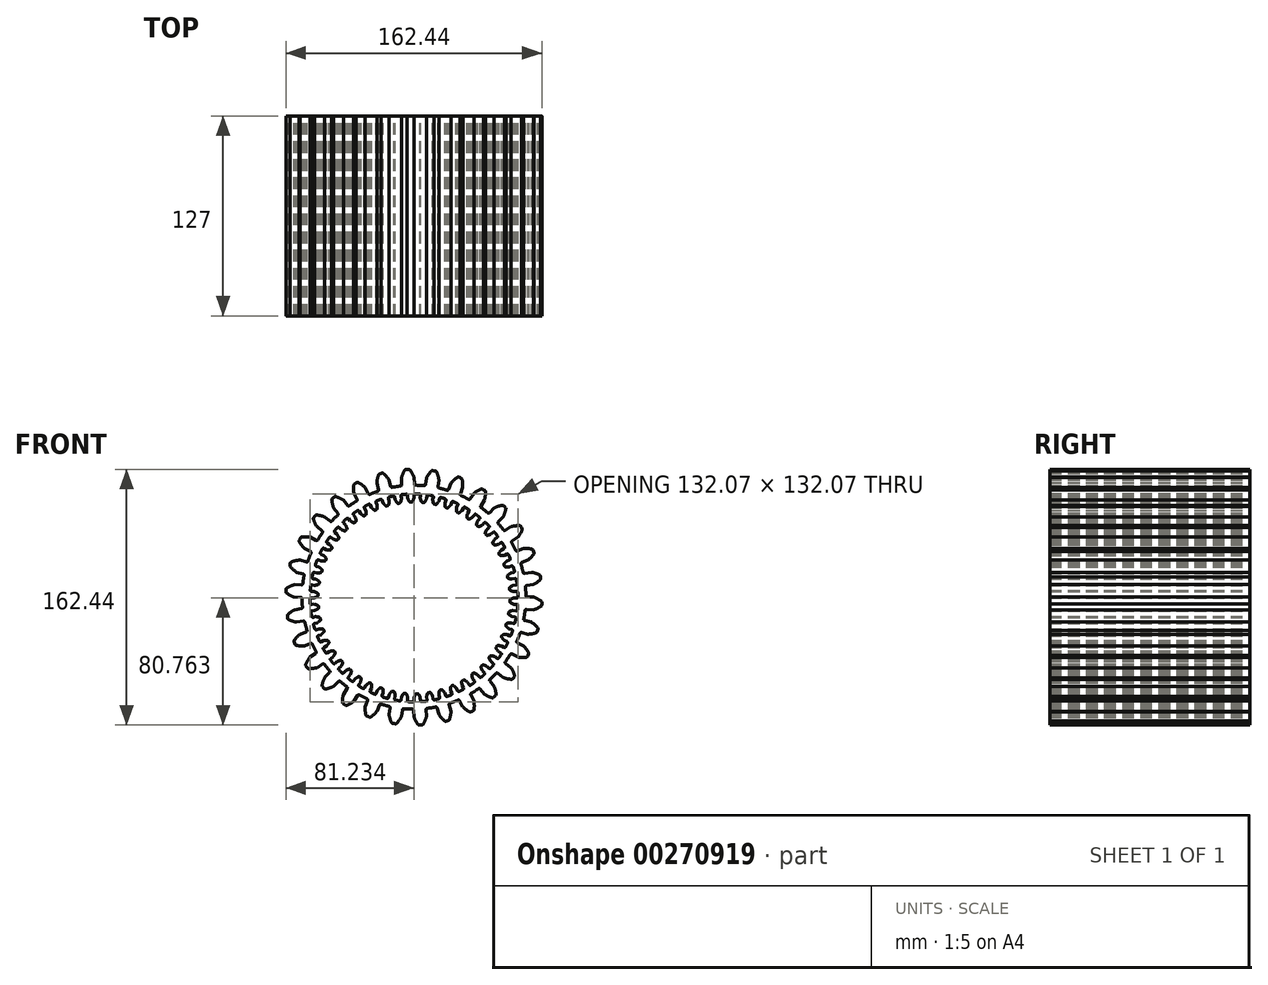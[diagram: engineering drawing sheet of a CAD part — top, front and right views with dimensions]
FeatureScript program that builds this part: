
annotation { "Feature Type Name" : "Feature", "Feature Type Description" : "" }
export const myFeature = defineFeature(function(context is Context, id is Id, definition is map)
    precondition{}
    {
        {
            var Q0;
            Q0=qCreatedBy(makeId("Front.planeOp"),FACE);
            var sketch = newSketch(context, id + "F0", { "sketchPlane" : qUnion([Q0])});
            skArc(sketch, "E0", {"start": v(-8.4, 70.62) * mm, "mid": v(-11.1, 70.25) * mm, "end": v(-13.76, 69.78) * mm});
            skArc(sketch, "E1.trimOffspring", {"start": v(0, 76.2) * mm, "mid": v(-1.15, 78.65) * mm, "end": v(-2.65, 80.92) * mm});
            skLineSegment(sketch, "E2", {"start": v(-3.28, 81.21) * mm, "end": v(-4.25, 81.18) * mm});
            skLineSegment(sketch, "E3", {"start": v(0, 76.2) * mm, "end": v(0.23, 71.9) * mm});
            skLineSegment(sketch, "E4.MirrorCS", {"start": v(-5.23, 81.11) * mm, "end": v(-4.25, 81.18) * mm});
            skArc(sketch, "E5.MirrorCS", {"start": v(-7.97, 75.78) * mm, "mid": v(-7.07, 78.34) * mm, "end": v(-5.83, 80.75) * mm});
            skLineSegment(sketch, "E6.MirrorCS", {"start": v(-7.97, 75.78) * mm, "end": v(-7.74, 71.42) * mm});
            skPoint(sketch, "E7.visualSharp", {"position": v(0.27, 71.12) * mm});
            skArc(sketch, "E7.filletArc", {"start": v(0.23, 71.9) * mm, "mid": v(0.48, 71.35) * mm, "end": v(1.05, 71.11) * mm});
            skPoint(sketch, "E8.visualSharp", {"position": v(-7.7, 70.7) * mm});
            skArc(sketch, "E8.filletArc", {"start": v(-8.4, 70.62) * mm, "mid": v(-7.91, 70.89) * mm, "end": v(-7.74, 71.42) * mm});
            skPoint(sketch, "E9.visualSharp", {"position": v(-5.62, 81.09) * mm});
            skArc(sketch, "E9.filletArc", {"start": v(-5.23, 81.11) * mm, "mid": v(-5.57, 81) * mm, "end": v(-5.83, 80.75) * mm});
            skPoint(sketch, "E10.visualSharp", {"position": v(-2.89, 81.23) * mm});
            skArc(sketch, "E10.filletArc", {"start": v(-2.65, 80.92) * mm, "mid": v(-2.93, 81.14) * mm, "end": v(-3.28, 81.21) * mm});
            skLineSegment(sketch, "E11.1.0", {"start": v(-21.98, 78.25) * mm, "end": v(-21.04, 78.52) * mm});
            skArc(sketch, "E11.1.1", {"start": v(-21.98, 78.25) * mm, "mid": v(-22.3, 78.08) * mm, "end": v(-22.49, 77.77) * mm});
            skLineSegment(sketch, "E11.1.2", {"start": v(-20.1, 78.76) * mm, "end": v(-21.04, 78.52) * mm});
            skArc(sketch, "E11.1.3", {"start": v(-19.41, 78.6) * mm, "mid": v(-19.73, 78.76) * mm, "end": v(-20.1, 78.76) * mm});
            skArc(sketch, "E11.1.4", {"start": v(-15.84, 74.53) * mm, "mid": v(-17.48, 76.7) * mm, "end": v(-19.41, 78.6) * mm});
            skLineSegment(sketch, "E11.1.5", {"start": v(-15.84, 74.53) * mm, "end": v(-14.73, 70.38) * mm});
            skLineSegment(sketch, "E11.1.6", {"start": v(-23.55, 72.47) * mm, "end": v(-22.42, 68.25) * mm});
            skArc(sketch, "E11.1.7", {"start": v(-22.9, 67.33) * mm, "mid": v(-22.48, 67.7) * mm, "end": v(-22.42, 68.25) * mm});
            skArc(sketch, "E11.1.8", {"start": v(-14.73, 70.38) * mm, "mid": v(-14.36, 69.89) * mm, "end": v(-13.76, 69.78) * mm});
            skArc(sketch, "E11.1.9", {"start": v(-23.55, 72.47) * mm, "mid": v(-23.2, 75.16) * mm, "end": v(-22.49, 77.77) * mm});
            skLineSegment(sketch, "E11.2.0", {"start": v(-37.77, 71.97) * mm, "end": v(-36.9, 72.43) * mm});
            skArc(sketch, "E11.2.1", {"start": v(-37.77, 71.97) * mm, "mid": v(-38.04, 71.73) * mm, "end": v(-38.17, 71.4) * mm});
            skLineSegment(sketch, "E11.2.2", {"start": v(-36.03, 72.86) * mm, "end": v(-36.9, 72.43) * mm});
            skArc(sketch, "E11.2.3", {"start": v(-35.33, 72.84) * mm, "mid": v(-35.68, 72.94) * mm, "end": v(-36.03, 72.86) * mm});
            skArc(sketch, "E11.2.4", {"start": v(-31, 69.61) * mm, "mid": v(-33.05, 71.38) * mm, "end": v(-35.33, 72.84) * mm});
            skLineSegment(sketch, "E11.2.5", {"start": v(-31, 69.61) * mm, "end": v(-29.04, 65.78) * mm});
            skLineSegment(sketch, "E11.2.6", {"start": v(-38.1, 66) * mm, "end": v(-36.12, 62.1) * mm});
            skArc(sketch, "E11.2.7", {"start": v(-36.4, 61.1) * mm, "mid": v(-36.06, 61.54) * mm, "end": v(-36.12, 62.1) * mm});
            skArc(sketch, "E11.2.8", {"start": v(-29.04, 65.78) * mm, "mid": v(-28.58, 65.37) * mm, "end": v(-27.97, 65.4) * mm});
            skArc(sketch, "E11.2.9", {"start": v(-38.1, 66) * mm, "mid": v(-38.33, 68.7) * mm, "end": v(-38.17, 71.4) * mm});
            skLineSegment(sketch, "E12.1.3.0", {"start": v(-51.9, 62.55) * mm, "end": v(-51.16, 63.18) * mm});
            skArc(sketch, "E12.3.3.0", {"start": v(-51.9, 62.55) * mm, "mid": v(-52.12, 62.26) * mm, "end": v(-52.18, 61.9) * mm});
            skLineSegment(sketch, "E12.7.3.0", {"start": v(-50.39, 63.78) * mm, "end": v(-51.16, 63.18) * mm});
            skArc(sketch, "E12.10.3.0", {"start": v(-49.7, 63.9) * mm, "mid": v(-50.06, 63.93) * mm, "end": v(-50.39, 63.78) * mm});
            skArc(sketch, "E12.14.3.0", {"start": v(-44.79, 61.65) * mm, "mid": v(-47.17, 62.95) * mm, "end": v(-49.7, 63.9) * mm});
            skLineSegment(sketch, "E12.18.3.0", {"start": v(-44.79, 61.65) * mm, "end": v(-42.08, 58.3) * mm});
            skLineSegment(sketch, "E12.21.3.0", {"start": v(-50.99, 56.63) * mm, "end": v(-48.24, 53.23) * mm});
            skArc(sketch, "E12.24.3.0", {"start": v(-48.31, 52.2) * mm, "mid": v(-48.07, 52.7) * mm, "end": v(-48.24, 53.23) * mm});
            skArc(sketch, "E12.28.3.0", {"start": v(-42.08, 58.3) * mm, "mid": v(-41.55, 58) * mm, "end": v(-40.95, 58.15) * mm});
            skArc(sketch, "E12.32.3.0", {"start": v(-50.99, 56.63) * mm, "mid": v(-51.77, 59.22) * mm, "end": v(-52.18, 61.9) * mm});
            skLineSegment(sketch, "E12.1.4.0", {"start": v(-63.78, 50.39) * mm, "end": v(-63.18, 51.16) * mm});
            skArc(sketch, "E12.3.4.0", {"start": v(-63.78, 50.39) * mm, "mid": v(-63.93, 50.06) * mm, "end": v(-63.9, 49.7) * mm});
            skLineSegment(sketch, "E12.7.4.0", {"start": v(-62.55, 51.9) * mm, "end": v(-63.18, 51.16) * mm});
            skArc(sketch, "E12.10.4.0", {"start": v(-61.9, 52.18) * mm, "mid": v(-62.26, 52.12) * mm, "end": v(-62.55, 51.9) * mm});
            skArc(sketch, "E12.14.4.0", {"start": v(-56.63, 50.99) * mm, "mid": v(-59.22, 51.77) * mm, "end": v(-61.9, 52.18) * mm});
            skLineSegment(sketch, "E12.18.4.0", {"start": v(-56.63, 50.99) * mm, "end": v(-53.28, 48.28) * mm});
            skLineSegment(sketch, "E12.21.4.0", {"start": v(-61.65, 44.79) * mm, "end": v(-58.25, 42.04) * mm});
            skArc(sketch, "E12.24.4.0", {"start": v(-58.1, 41) * mm, "mid": v(-57.98, 41.55) * mm, "end": v(-58.25, 42.04) * mm});
            skArc(sketch, "E12.28.4.0", {"start": v(-53.28, 48.28) * mm, "mid": v(-52.7, 48.1) * mm, "end": v(-52.15, 48.36) * mm});
            skArc(sketch, "E12.32.4.0", {"start": v(-61.65, 44.79) * mm, "mid": v(-62.95, 47.17) * mm, "end": v(-63.9, 49.7) * mm});
            skLineSegment(sketch, "E12.1.5.0", {"start": v(-72.86, 36.03) * mm, "end": v(-72.43, 36.9) * mm});
            skArc(sketch, "E12.3.5.0", {"start": v(-72.86, 36.03) * mm, "mid": v(-72.94, 35.68) * mm, "end": v(-72.84, 35.33) * mm});
            skLineSegment(sketch, "E12.7.5.0", {"start": v(-71.97, 37.77) * mm, "end": v(-72.43, 36.9) * mm});
            skArc(sketch, "E12.10.5.0", {"start": v(-71.4, 38.17) * mm, "mid": v(-71.73, 38.04) * mm, "end": v(-71.97, 37.77) * mm});
            skArc(sketch, "E12.14.5.0", {"start": v(-66, 38.1) * mm, "mid": v(-68.7, 38.33) * mm, "end": v(-71.4, 38.17) * mm});
            skLineSegment(sketch, "E12.18.5.0", {"start": v(-66, 38.1) * mm, "end": v(-62.16, 36.15) * mm});
            skLineSegment(sketch, "E12.21.5.0", {"start": v(-69.61, 31) * mm, "end": v(-65.72, 29) * mm});
            skArc(sketch, "E12.24.5.0", {"start": v(-65.36, 28.03) * mm, "mid": v(-65.35, 28.59) * mm, "end": v(-65.72, 29) * mm});
            skArc(sketch, "E12.28.5.0", {"start": v(-62.16, 36.15) * mm, "mid": v(-61.55, 36.09) * mm, "end": v(-61.06, 36.46) * mm});
            skArc(sketch, "E12.32.5.0", {"start": v(-69.61, 31) * mm, "mid": v(-71.38, 33.05) * mm, "end": v(-72.84, 35.33) * mm});
            skLineSegment(sketch, "E12.1.6.0", {"start": v(-78.76, 20.1) * mm, "end": v(-78.52, 21.04) * mm});
            skArc(sketch, "E12.3.6.0", {"start": v(-78.76, 20.1) * mm, "mid": v(-78.76, 19.73) * mm, "end": v(-78.6, 19.41) * mm});
            skLineSegment(sketch, "E12.7.6.0", {"start": v(-78.25, 21.98) * mm, "end": v(-78.52, 21.04) * mm});
            skArc(sketch, "E12.10.6.0", {"start": v(-77.77, 22.49) * mm, "mid": v(-78.08, 22.3) * mm, "end": v(-78.25, 21.98) * mm});
            skArc(sketch, "E12.14.6.0", {"start": v(-72.47, 23.55) * mm, "mid": v(-75.16, 23.2) * mm, "end": v(-77.77, 22.49) * mm});
            skLineSegment(sketch, "E12.18.6.0", {"start": v(-72.47, 23.55) * mm, "end": v(-68.32, 22.43) * mm});
            skLineSegment(sketch, "E12.21.6.0", {"start": v(-74.53, 15.84) * mm, "end": v(-70.31, 14.71) * mm});
            skArc(sketch, "E12.24.6.0", {"start": v(-69.76, 13.83) * mm, "mid": v(-69.86, 14.38) * mm, "end": v(-70.31, 14.71) * mm});
            skArc(sketch, "E12.28.6.0", {"start": v(-68.32, 22.43) * mm, "mid": v(-67.7, 22.5) * mm, "end": v(-67.3, 22.97) * mm});
            skArc(sketch, "E12.32.6.0", {"start": v(-74.53, 15.84) * mm, "mid": v(-76.7, 17.48) * mm, "end": v(-78.6, 19.41) * mm});
            skLineSegment(sketch, "E12.1.7.0", {"start": v(-81.21, 3.28) * mm, "end": v(-81.18, 4.25) * mm});
            skArc(sketch, "E12.3.7.0", {"start": v(-81.21, 3.28) * mm, "mid": v(-81.14, 2.93) * mm, "end": v(-80.92, 2.65) * mm});
            skLineSegment(sketch, "E12.7.7.0", {"start": v(-81.11, 5.23) * mm, "end": v(-81.18, 4.25) * mm});
            skArc(sketch, "E12.10.7.0", {"start": v(-80.75, 5.83) * mm, "mid": v(-81, 5.57) * mm, "end": v(-81.11, 5.23) * mm});
            skArc(sketch, "E12.14.7.0", {"start": v(-75.78, 7.97) * mm, "mid": v(-78.34, 7.07) * mm, "end": v(-80.75, 5.83) * mm});
            skLineSegment(sketch, "E12.18.7.0", {"start": v(-75.78, 7.97) * mm, "end": v(-71.49, 7.74) * mm});
            skLineSegment(sketch, "E12.21.7.0", {"start": v(-76.2, 0) * mm, "end": v(-71.84, -0.23) * mm});
            skArc(sketch, "E12.24.7.0", {"start": v(-71.11, -0.98) * mm, "mid": v(-71.33, -0.46) * mm, "end": v(-71.84, -0.23) * mm});
            skArc(sketch, "E12.28.7.0", {"start": v(-71.49, 7.74) * mm, "mid": v(-70.9, 7.94) * mm, "end": v(-70.61, 8.48) * mm});
            skArc(sketch, "E12.32.7.0", {"start": v(-76.2, 0) * mm, "mid": v(-78.65, 1.15) * mm, "end": v(-80.92, 2.65) * mm});
            skLineSegment(sketch, "E12.1.8.0", {"start": v(-80.12, -13.68) * mm, "end": v(-80.3, -12.72) * mm});
            skArc(sketch, "E12.3.8.0", {"start": v(-80.12, -13.68) * mm, "mid": v(-79.98, -14) * mm, "end": v(-79.7, -14.24) * mm});
            skLineSegment(sketch, "E12.7.8.0", {"start": v(-80.43, -11.75) * mm, "end": v(-80.3, -12.72) * mm});
            skArc(sketch, "E12.10.8.0", {"start": v(-80.2, -11.09) * mm, "mid": v(-80.4, -11.4) * mm, "end": v(-80.43, -11.75) * mm});
            skArc(sketch, "E12.14.8.0", {"start": v(-75.78, -7.97) * mm, "mid": v(-78.1, -9.37) * mm, "end": v(-80.2, -11.09) * mm});
            skLineSegment(sketch, "E12.18.8.0", {"start": v(-75.78, -7.97) * mm, "end": v(-71.53, -7.3) * mm});
            skLineSegment(sketch, "E12.21.8.0", {"start": v(-74.53, -15.84) * mm, "end": v(-70.22, -15.16) * mm});
            skArc(sketch, "E12.24.8.0", {"start": v(-69.36, -15.74) * mm, "mid": v(-69.67, -15.28) * mm, "end": v(-70.22, -15.16) * mm});
            skArc(sketch, "E12.28.8.0", {"start": v(-71.53, -7.3) * mm, "mid": v(-71, -6.98) * mm, "end": v(-70.83, -6.4) * mm});
            skArc(sketch, "E12.32.8.0", {"start": v(-74.53, -15.84) * mm, "mid": v(-77.17, -15.22) * mm, "end": v(-79.7, -14.24) * mm});
            skLineSegment(sketch, "E12.1.9.0", {"start": v(-75.53, -30.04) * mm, "end": v(-75.9, -29.13) * mm});
            skArc(sketch, "E12.3.9.0", {"start": v(-75.53, -30.04) * mm, "mid": v(-75.32, -30.33) * mm, "end": v(-75, -30.5) * mm});
            skLineSegment(sketch, "E12.7.9.0", {"start": v(-76.23, -28.21) * mm, "end": v(-75.9, -29.13) * mm});
            skArc(sketch, "E12.10.9.0", {"start": v(-76.14, -27.52) * mm, "mid": v(-76.27, -27.86) * mm, "end": v(-76.23, -28.21) * mm});
            skArc(sketch, "E12.14.9.0", {"start": v(-72.47, -23.55) * mm, "mid": v(-74.45, -25.4) * mm, "end": v(-76.14, -27.52) * mm});
            skLineSegment(sketch, "E12.18.9.0", {"start": v(-72.47, -23.55) * mm, "end": v(-68.45, -22) * mm});
            skLineSegment(sketch, "E12.21.9.0", {"start": v(-69.61, -31) * mm, "end": v(-65.53, -29.43) * mm});
            skArc(sketch, "E12.24.9.0", {"start": v(-64.57, -29.82) * mm, "mid": v(-64.97, -29.43) * mm, "end": v(-65.53, -29.43) * mm});
            skArc(sketch, "E12.28.9.0", {"start": v(-68.45, -22) * mm, "mid": v(-68, -21.6) * mm, "end": v(-67.96, -20.98) * mm});
            skArc(sketch, "E12.32.9.0", {"start": v(-69.61, -31) * mm, "mid": v(-72.32, -30.94) * mm, "end": v(-75, -30.5) * mm});
            skLineSegment(sketch, "E12.1.10.0", {"start": v(-67.63, -45.09) * mm, "end": v(-68.18, -44.27) * mm});
            skArc(sketch, "E12.3.10.0", {"start": v(-67.63, -45.09) * mm, "mid": v(-67.37, -45.33) * mm, "end": v(-67.02, -45.42) * mm});
            skLineSegment(sketch, "E12.7.10.0", {"start": v(-68.7, -43.45) * mm, "end": v(-68.18, -44.27) * mm});
            skArc(sketch, "E12.10.10.0", {"start": v(-68.75, -42.75) * mm, "mid": v(-68.8, -43.1) * mm, "end": v(-68.7, -43.45) * mm});
            skArc(sketch, "E12.14.10.0", {"start": v(-66, -38.1) * mm, "mid": v(-67.54, -40.33) * mm, "end": v(-68.75, -42.75) * mm});
            skLineSegment(sketch, "E12.18.10.0", {"start": v(-66, -38.1) * mm, "end": v(-62.38, -35.76) * mm});
            skLineSegment(sketch, "E12.21.10.0", {"start": v(-61.65, -44.79) * mm, "end": v(-57.98, -42.4) * mm});
            skArc(sketch, "E12.24.10.0", {"start": v(-56.96, -42.6) * mm, "mid": v(-57.43, -42.3) * mm, "end": v(-57.98, -42.4) * mm});
            skArc(sketch, "E12.28.10.0", {"start": v(-62.38, -35.76) * mm, "mid": v(-62.03, -35.26) * mm, "end": v(-62.1, -34.65) * mm});
            skArc(sketch, "E12.32.10.0", {"start": v(-61.65, -44.79) * mm, "mid": v(-64.31, -45.3) * mm, "end": v(-67.02, -45.42) * mm});
            skLineSegment(sketch, "E12.1.11.0", {"start": v(-56.78, -58.16) * mm, "end": v(-57.48, -57.48) * mm});
            skArc(sketch, "E12.3.11.0", {"start": v(-56.78, -58.16) * mm, "mid": v(-56.47, -58.34) * mm, "end": v(-56.11, -58.36) * mm});
            skLineSegment(sketch, "E12.7.11.0", {"start": v(-58.16, -56.78) * mm, "end": v(-57.48, -57.48) * mm});
            skArc(sketch, "E12.10.11.0", {"start": v(-58.36, -56.11) * mm, "mid": v(-58.34, -56.47) * mm, "end": v(-58.16, -56.78) * mm});
            skArc(sketch, "E12.14.11.0", {"start": v(-56.63, -50.99) * mm, "mid": v(-57.68, -53.49) * mm, "end": v(-58.36, -56.11) * mm});
            skLineSegment(sketch, "E12.18.11.0", {"start": v(-56.63, -50.99) * mm, "end": v(-53.59, -47.95) * mm});
            skLineSegment(sketch, "E12.21.11.0", {"start": v(-50.99, -56.63) * mm, "end": v(-47.9, -53.54) * mm});
            skArc(sketch, "E12.24.11.0", {"start": v(-46.86, -53.5) * mm, "mid": v(-47.38, -53.31) * mm, "end": v(-47.9, -53.54) * mm});
            skArc(sketch, "E12.28.11.0", {"start": v(-53.59, -47.95) * mm, "mid": v(-53.34, -47.38) * mm, "end": v(-53.55, -46.8) * mm});
            skArc(sketch, "E12.32.11.0", {"start": v(-50.99, -56.63) * mm, "mid": v(-53.49, -57.68) * mm, "end": v(-56.11, -58.36) * mm});
            skLineSegment(sketch, "E12.1.12.0", {"start": v(-43.45, -68.7) * mm, "end": v(-44.27, -68.18) * mm});
            skArc(sketch, "E12.3.12.0", {"start": v(-43.45, -68.7) * mm, "mid": v(-43.1, -68.8) * mm, "end": v(-42.75, -68.75) * mm});
            skLineSegment(sketch, "E12.7.12.0", {"start": v(-45.09, -67.63) * mm, "end": v(-44.27, -68.18) * mm});
            skArc(sketch, "E12.10.12.0", {"start": v(-45.42, -67.02) * mm, "mid": v(-45.33, -67.37) * mm, "end": v(-45.09, -67.63) * mm});
            skArc(sketch, "E12.14.12.0", {"start": v(-44.79, -61.65) * mm, "mid": v(-45.3, -64.31) * mm, "end": v(-45.42, -67.02) * mm});
            skLineSegment(sketch, "E12.18.12.0", {"start": v(-44.79, -61.65) * mm, "end": v(-42.45, -58.04) * mm});
            skLineSegment(sketch, "E12.21.12.0", {"start": v(-38.1, -66) * mm, "end": v(-35.72, -62.33) * mm});
            skArc(sketch, "E12.24.12.0", {"start": v(-34.7, -62.08) * mm, "mid": v(-35.26, -62) * mm, "end": v(-35.72, -62.33) * mm});
            skArc(sketch, "E12.28.12.0", {"start": v(-42.45, -58.04) * mm, "mid": v(-42.32, -57.44) * mm, "end": v(-42.65, -56.92) * mm});
            skArc(sketch, "E12.32.12.0", {"start": v(-38.1, -66) * mm, "mid": v(-40.33, -67.54) * mm, "end": v(-42.75, -68.75) * mm});
            skLineSegment(sketch, "E12.1.13.0", {"start": v(-28.21, -76.23) * mm, "end": v(-29.13, -75.9) * mm});
            skArc(sketch, "E12.3.13.0", {"start": v(-28.21, -76.23) * mm, "mid": v(-27.86, -76.27) * mm, "end": v(-27.52, -76.14) * mm});
            skLineSegment(sketch, "E12.7.13.0", {"start": v(-30.04, -75.53) * mm, "end": v(-29.13, -75.9) * mm});
            skArc(sketch, "E12.10.13.0", {"start": v(-30.5, -75) * mm, "mid": v(-30.33, -75.32) * mm, "end": v(-30.04, -75.53) * mm});
            skArc(sketch, "E12.14.13.0", {"start": v(-31, -69.61) * mm, "mid": v(-30.94, -72.32) * mm, "end": v(-30.5, -75) * mm});
            skLineSegment(sketch, "E12.18.13.0", {"start": v(-31, -69.61) * mm, "end": v(-29.45, -65.6) * mm});
            skLineSegment(sketch, "E12.21.13.0", {"start": v(-23.55, -72.47) * mm, "end": v(-21.98, -68.4) * mm});
            skArc(sketch, "E12.24.13.0", {"start": v(-21.04, -67.94) * mm, "mid": v(-21.6, -67.98) * mm, "end": v(-21.98, -68.4) * mm});
            skArc(sketch, "E12.28.13.0", {"start": v(-29.45, -65.6) * mm, "mid": v(-29.46, -64.98) * mm, "end": v(-29.88, -64.54) * mm});
            skArc(sketch, "E12.32.13.0", {"start": v(-23.55, -72.47) * mm, "mid": v(-25.4, -74.45) * mm, "end": v(-27.52, -76.14) * mm});
            skLineSegment(sketch, "E12.1.14.0", {"start": v(-11.75, -80.43) * mm, "end": v(-12.72, -80.3) * mm});
            skArc(sketch, "E12.3.14.0", {"start": v(-11.75, -80.43) * mm, "mid": v(-11.4, -80.4) * mm, "end": v(-11.09, -80.2) * mm});
            skLineSegment(sketch, "E12.7.14.0", {"start": v(-13.68, -80.12) * mm, "end": v(-12.72, -80.3) * mm});
            skArc(sketch, "E12.10.14.0", {"start": v(-14.24, -79.7) * mm, "mid": v(-14, -79.98) * mm, "end": v(-13.68, -80.12) * mm});
            skArc(sketch, "E12.14.14.0", {"start": v(-15.84, -74.53) * mm, "mid": v(-15.22, -77.17) * mm, "end": v(-14.24, -79.7) * mm});
            skLineSegment(sketch, "E12.18.14.0", {"start": v(-15.84, -74.53) * mm, "end": v(-15.17, -70.29) * mm});
            skLineSegment(sketch, "E12.21.14.0", {"start": v(-7.97, -75.78) * mm, "end": v(-7.28, -71.47) * mm});
            skArc(sketch, "E12.24.14.0", {"start": v(-6.46, -70.83) * mm, "mid": v(-7, -70.98) * mm, "end": v(-7.28, -71.47) * mm});
            skArc(sketch, "E12.28.14.0", {"start": v(-15.17, -70.29) * mm, "mid": v(-15.3, -69.69) * mm, "end": v(-15.8, -69.34) * mm});
            skArc(sketch, "E12.32.14.0", {"start": v(-7.97, -75.78) * mm, "mid": v(-9.37, -78.1) * mm, "end": v(-11.09, -80.2) * mm});
            skLineSegment(sketch, "E12.1.15.0", {"start": v(5.23, -81.11) * mm, "end": v(4.25, -81.18) * mm});
            skArc(sketch, "E12.3.15.0", {"start": v(5.23, -81.11) * mm, "mid": v(5.57, -81) * mm, "end": v(5.83, -80.75) * mm});
            skLineSegment(sketch, "E12.7.15.0", {"start": v(3.28, -81.21) * mm, "end": v(4.25, -81.18) * mm});
            skArc(sketch, "E12.10.15.0", {"start": v(2.65, -80.92) * mm, "mid": v(2.93, -81.14) * mm, "end": v(3.28, -81.21) * mm});
            skArc(sketch, "E12.14.15.0", {"start": v(0, -76.2) * mm, "mid": v(1.15, -78.65) * mm, "end": v(2.65, -80.92) * mm});
            skLineSegment(sketch, "E12.18.15.0", {"start": v(0, -76.2) * mm, "end": v(-0.23, -71.9) * mm});
            skLineSegment(sketch, "E12.21.15.0", {"start": v(7.97, -75.78) * mm, "end": v(7.74, -71.42) * mm});
            skArc(sketch, "E12.24.15.0", {"start": v(8.4, -70.62) * mm, "mid": v(7.91, -70.89) * mm, "end": v(7.74, -71.42) * mm});
            skArc(sketch, "E12.28.15.0", {"start": v(-0.23, -71.9) * mm, "mid": v(-0.48, -71.35) * mm, "end": v(-1.05, -71.11) * mm});
            skArc(sketch, "E12.32.15.0", {"start": v(7.97, -75.78) * mm, "mid": v(7.07, -78.34) * mm, "end": v(5.83, -80.75) * mm});
            skLineSegment(sketch, "E12.1.16.0", {"start": v(21.98, -78.25) * mm, "end": v(21.04, -78.52) * mm});
            skArc(sketch, "E12.3.16.0", {"start": v(21.98, -78.25) * mm, "mid": v(22.3, -78.08) * mm, "end": v(22.49, -77.77) * mm});
            skLineSegment(sketch, "E12.7.16.0", {"start": v(20.1, -78.76) * mm, "end": v(21.04, -78.52) * mm});
            skArc(sketch, "E12.10.16.0", {"start": v(19.41, -78.6) * mm, "mid": v(19.73, -78.76) * mm, "end": v(20.1, -78.76) * mm});
            skArc(sketch, "E12.14.16.0", {"start": v(15.84, -74.53) * mm, "mid": v(17.48, -76.7) * mm, "end": v(19.41, -78.6) * mm});
            skLineSegment(sketch, "E12.18.16.0", {"start": v(15.84, -74.53) * mm, "end": v(14.73, -70.38) * mm});
            skLineSegment(sketch, "E12.21.16.0", {"start": v(23.55, -72.47) * mm, "end": v(22.42, -68.25) * mm});
            skArc(sketch, "E12.24.16.0", {"start": v(22.9, -67.33) * mm, "mid": v(22.48, -67.7) * mm, "end": v(22.42, -68.25) * mm});
            skArc(sketch, "E12.28.16.0", {"start": v(14.73, -70.38) * mm, "mid": v(14.36, -69.89) * mm, "end": v(13.76, -69.78) * mm});
            skArc(sketch, "E12.32.16.0", {"start": v(23.55, -72.47) * mm, "mid": v(23.2, -75.16) * mm, "end": v(22.49, -77.77) * mm});
            skLineSegment(sketch, "E12.1.17.0", {"start": v(37.77, -71.97) * mm, "end": v(36.9, -72.43) * mm});
            skArc(sketch, "E12.3.17.0", {"start": v(37.77, -71.97) * mm, "mid": v(38.04, -71.73) * mm, "end": v(38.17, -71.4) * mm});
            skLineSegment(sketch, "E12.7.17.0", {"start": v(36.03, -72.86) * mm, "end": v(36.9, -72.43) * mm});
            skArc(sketch, "E12.10.17.0", {"start": v(35.33, -72.84) * mm, "mid": v(35.68, -72.94) * mm, "end": v(36.03, -72.86) * mm});
            skArc(sketch, "E12.14.17.0", {"start": v(31, -69.61) * mm, "mid": v(33.05, -71.38) * mm, "end": v(35.33, -72.84) * mm});
            skLineSegment(sketch, "E12.18.17.0", {"start": v(31, -69.61) * mm, "end": v(29.04, -65.78) * mm});
            skLineSegment(sketch, "E12.21.17.0", {"start": v(38.1, -66) * mm, "end": v(36.12, -62.1) * mm});
            skArc(sketch, "E12.24.17.0", {"start": v(36.4, -61.1) * mm, "mid": v(36.06, -61.54) * mm, "end": v(36.12, -62.1) * mm});
            skArc(sketch, "E12.28.17.0", {"start": v(29.04, -65.78) * mm, "mid": v(28.58, -65.37) * mm, "end": v(27.97, -65.4) * mm});
            skArc(sketch, "E12.32.17.0", {"start": v(38.1, -66) * mm, "mid": v(38.33, -68.7) * mm, "end": v(38.17, -71.4) * mm});
            skLineSegment(sketch, "E12.1.18.0", {"start": v(51.9, -62.55) * mm, "end": v(51.16, -63.18) * mm});
            skArc(sketch, "E12.3.18.0", {"start": v(51.9, -62.55) * mm, "mid": v(52.12, -62.26) * mm, "end": v(52.18, -61.9) * mm});
            skLineSegment(sketch, "E12.7.18.0", {"start": v(50.39, -63.78) * mm, "end": v(51.16, -63.18) * mm});
            skArc(sketch, "E12.10.18.0", {"start": v(49.7, -63.9) * mm, "mid": v(50.06, -63.93) * mm, "end": v(50.39, -63.78) * mm});
            skArc(sketch, "E12.14.18.0", {"start": v(44.79, -61.65) * mm, "mid": v(47.17, -62.95) * mm, "end": v(49.7, -63.9) * mm});
            skLineSegment(sketch, "E12.18.18.0", {"start": v(44.79, -61.65) * mm, "end": v(42.08, -58.3) * mm});
            skLineSegment(sketch, "E12.21.18.0", {"start": v(50.99, -56.63) * mm, "end": v(48.24, -53.23) * mm});
            skArc(sketch, "E12.24.18.0", {"start": v(48.31, -52.2) * mm, "mid": v(48.07, -52.7) * mm, "end": v(48.24, -53.23) * mm});
            skArc(sketch, "E12.28.18.0", {"start": v(42.08, -58.3) * mm, "mid": v(41.55, -58) * mm, "end": v(40.95, -58.15) * mm});
            skArc(sketch, "E12.32.18.0", {"start": v(50.99, -56.63) * mm, "mid": v(51.77, -59.22) * mm, "end": v(52.18, -61.9) * mm});
            skLineSegment(sketch, "E12.1.19.0", {"start": v(63.78, -50.39) * mm, "end": v(63.18, -51.16) * mm});
            skArc(sketch, "E12.3.19.0", {"start": v(63.78, -50.39) * mm, "mid": v(63.93, -50.06) * mm, "end": v(63.9, -49.7) * mm});
            skLineSegment(sketch, "E12.7.19.0", {"start": v(62.55, -51.9) * mm, "end": v(63.18, -51.16) * mm});
            skArc(sketch, "E12.10.19.0", {"start": v(61.9, -52.18) * mm, "mid": v(62.26, -52.12) * mm, "end": v(62.55, -51.9) * mm});
            skArc(sketch, "E12.14.19.0", {"start": v(56.63, -50.99) * mm, "mid": v(59.22, -51.77) * mm, "end": v(61.9, -52.18) * mm});
            skLineSegment(sketch, "E12.18.19.0", {"start": v(56.63, -50.99) * mm, "end": v(53.28, -48.28) * mm});
            skLineSegment(sketch, "E12.21.19.0", {"start": v(61.65, -44.79) * mm, "end": v(58.25, -42.04) * mm});
            skArc(sketch, "E12.24.19.0", {"start": v(58.1, -41) * mm, "mid": v(57.98, -41.55) * mm, "end": v(58.25, -42.04) * mm});
            skArc(sketch, "E12.28.19.0", {"start": v(53.28, -48.28) * mm, "mid": v(52.7, -48.1) * mm, "end": v(52.15, -48.36) * mm});
            skArc(sketch, "E12.32.19.0", {"start": v(61.65, -44.79) * mm, "mid": v(62.95, -47.17) * mm, "end": v(63.9, -49.7) * mm});
            skLineSegment(sketch, "E12.1.20.0", {"start": v(72.86, -36.03) * mm, "end": v(72.43, -36.9) * mm});
            skArc(sketch, "E12.3.20.0", {"start": v(72.86, -36.03) * mm, "mid": v(72.94, -35.68) * mm, "end": v(72.84, -35.33) * mm});
            skLineSegment(sketch, "E12.7.20.0", {"start": v(71.97, -37.77) * mm, "end": v(72.43, -36.9) * mm});
            skArc(sketch, "E12.10.20.0", {"start": v(71.4, -38.17) * mm, "mid": v(71.73, -38.04) * mm, "end": v(71.97, -37.77) * mm});
            skArc(sketch, "E12.14.20.0", {"start": v(66, -38.1) * mm, "mid": v(68.7, -38.33) * mm, "end": v(71.4, -38.17) * mm});
            skLineSegment(sketch, "E12.18.20.0", {"start": v(66, -38.1) * mm, "end": v(62.16, -36.15) * mm});
            skLineSegment(sketch, "E12.21.20.0", {"start": v(69.61, -31) * mm, "end": v(65.72, -29) * mm});
            skArc(sketch, "E12.24.20.0", {"start": v(65.36, -28.03) * mm, "mid": v(65.35, -28.59) * mm, "end": v(65.72, -29) * mm});
            skArc(sketch, "E12.28.20.0", {"start": v(62.16, -36.15) * mm, "mid": v(61.55, -36.09) * mm, "end": v(61.06, -36.46) * mm});
            skArc(sketch, "E12.32.20.0", {"start": v(69.61, -31) * mm, "mid": v(71.38, -33.05) * mm, "end": v(72.84, -35.33) * mm});
            skLineSegment(sketch, "E12.1.21.0", {"start": v(78.76, -20.1) * mm, "end": v(78.52, -21.04) * mm});
            skArc(sketch, "E12.3.21.0", {"start": v(78.76, -20.1) * mm, "mid": v(78.76, -19.73) * mm, "end": v(78.6, -19.41) * mm});
            skLineSegment(sketch, "E12.7.21.0", {"start": v(78.25, -21.98) * mm, "end": v(78.52, -21.04) * mm});
            skArc(sketch, "E12.10.21.0", {"start": v(77.77, -22.49) * mm, "mid": v(78.08, -22.3) * mm, "end": v(78.25, -21.98) * mm});
            skArc(sketch, "E12.14.21.0", {"start": v(72.47, -23.55) * mm, "mid": v(75.16, -23.2) * mm, "end": v(77.77, -22.49) * mm});
            skLineSegment(sketch, "E12.18.21.0", {"start": v(72.47, -23.55) * mm, "end": v(68.32, -22.43) * mm});
            skLineSegment(sketch, "E12.21.21.0", {"start": v(74.53, -15.84) * mm, "end": v(70.31, -14.71) * mm});
            skArc(sketch, "E12.24.21.0", {"start": v(69.76, -13.83) * mm, "mid": v(69.86, -14.38) * mm, "end": v(70.31, -14.71) * mm});
            skArc(sketch, "E12.28.21.0", {"start": v(68.32, -22.43) * mm, "mid": v(67.7, -22.5) * mm, "end": v(67.3, -22.97) * mm});
            skArc(sketch, "E12.32.21.0", {"start": v(74.53, -15.84) * mm, "mid": v(76.7, -17.48) * mm, "end": v(78.6, -19.41) * mm});
            skLineSegment(sketch, "E12.1.22.0", {"start": v(81.21, -3.28) * mm, "end": v(81.18, -4.25) * mm});
            skArc(sketch, "E12.3.22.0", {"start": v(81.21, -3.28) * mm, "mid": v(81.14, -2.93) * mm, "end": v(80.92, -2.65) * mm});
            skLineSegment(sketch, "E12.7.22.0", {"start": v(81.11, -5.23) * mm, "end": v(81.18, -4.25) * mm});
            skArc(sketch, "E12.10.22.0", {"start": v(80.75, -5.83) * mm, "mid": v(81, -5.57) * mm, "end": v(81.11, -5.23) * mm});
            skArc(sketch, "E12.14.22.0", {"start": v(75.78, -7.97) * mm, "mid": v(78.34, -7.07) * mm, "end": v(80.75, -5.83) * mm});
            skLineSegment(sketch, "E12.18.22.0", {"start": v(75.78, -7.97) * mm, "end": v(71.49, -7.74) * mm});
            skLineSegment(sketch, "E12.21.22.0", {"start": v(76.2, 0) * mm, "end": v(71.84, 0.23) * mm});
            skArc(sketch, "E12.24.22.0", {"start": v(71.11, 0.98) * mm, "mid": v(71.33, 0.46) * mm, "end": v(71.84, 0.23) * mm});
            skArc(sketch, "E12.28.22.0", {"start": v(71.49, -7.74) * mm, "mid": v(70.9, -7.94) * mm, "end": v(70.61, -8.48) * mm});
            skArc(sketch, "E12.32.22.0", {"start": v(76.2, 0) * mm, "mid": v(78.65, -1.15) * mm, "end": v(80.92, -2.65) * mm});
            skLineSegment(sketch, "E12.1.23.0", {"start": v(80.12, 13.68) * mm, "end": v(80.3, 12.72) * mm});
            skArc(sketch, "E12.3.23.0", {"start": v(80.12, 13.68) * mm, "mid": v(79.98, 14) * mm, "end": v(79.7, 14.24) * mm});
            skLineSegment(sketch, "E12.7.23.0", {"start": v(80.43, 11.75) * mm, "end": v(80.3, 12.72) * mm});
            skArc(sketch, "E12.10.23.0", {"start": v(80.2, 11.09) * mm, "mid": v(80.4, 11.4) * mm, "end": v(80.43, 11.75) * mm});
            skArc(sketch, "E12.14.23.0", {"start": v(75.78, 7.97) * mm, "mid": v(78.1, 9.37) * mm, "end": v(80.2, 11.09) * mm});
            skLineSegment(sketch, "E12.18.23.0", {"start": v(75.78, 7.97) * mm, "end": v(71.53, 7.3) * mm});
            skLineSegment(sketch, "E12.21.23.0", {"start": v(74.53, 15.84) * mm, "end": v(70.22, 15.16) * mm});
            skArc(sketch, "E12.24.23.0", {"start": v(69.36, 15.74) * mm, "mid": v(69.67, 15.28) * mm, "end": v(70.22, 15.16) * mm});
            skArc(sketch, "E12.28.23.0", {"start": v(71.53, 7.3) * mm, "mid": v(71, 6.98) * mm, "end": v(70.83, 6.4) * mm});
            skArc(sketch, "E12.32.23.0", {"start": v(74.53, 15.84) * mm, "mid": v(77.17, 15.22) * mm, "end": v(79.7, 14.24) * mm});
            skLineSegment(sketch, "E12.1.24.0", {"start": v(75.53, 30.04) * mm, "end": v(75.9, 29.13) * mm});
            skArc(sketch, "E12.3.24.0", {"start": v(75.53, 30.04) * mm, "mid": v(75.32, 30.33) * mm, "end": v(75, 30.5) * mm});
            skLineSegment(sketch, "E12.7.24.0", {"start": v(76.23, 28.21) * mm, "end": v(75.9, 29.13) * mm});
            skArc(sketch, "E12.10.24.0", {"start": v(76.14, 27.52) * mm, "mid": v(76.27, 27.86) * mm, "end": v(76.23, 28.21) * mm});
            skArc(sketch, "E12.14.24.0", {"start": v(72.47, 23.55) * mm, "mid": v(74.45, 25.4) * mm, "end": v(76.14, 27.52) * mm});
            skLineSegment(sketch, "E12.18.24.0", {"start": v(72.47, 23.55) * mm, "end": v(68.45, 22) * mm});
            skLineSegment(sketch, "E12.21.24.0", {"start": v(69.61, 31) * mm, "end": v(65.53, 29.43) * mm});
            skArc(sketch, "E12.24.24.0", {"start": v(64.57, 29.82) * mm, "mid": v(64.97, 29.43) * mm, "end": v(65.53, 29.43) * mm});
            skArc(sketch, "E12.28.24.0", {"start": v(68.45, 22) * mm, "mid": v(68, 21.6) * mm, "end": v(67.96, 20.98) * mm});
            skArc(sketch, "E12.32.24.0", {"start": v(69.61, 31) * mm, "mid": v(72.32, 30.94) * mm, "end": v(75, 30.5) * mm});
            skLineSegment(sketch, "E12.1.25.0", {"start": v(67.63, 45.09) * mm, "end": v(68.18, 44.27) * mm});
            skArc(sketch, "E12.3.25.0", {"start": v(67.63, 45.09) * mm, "mid": v(67.37, 45.33) * mm, "end": v(67.02, 45.42) * mm});
            skLineSegment(sketch, "E12.7.25.0", {"start": v(68.7, 43.45) * mm, "end": v(68.18, 44.27) * mm});
            skArc(sketch, "E12.10.25.0", {"start": v(68.75, 42.75) * mm, "mid": v(68.8, 43.1) * mm, "end": v(68.7, 43.45) * mm});
            skArc(sketch, "E12.14.25.0", {"start": v(66, 38.1) * mm, "mid": v(67.54, 40.33) * mm, "end": v(68.75, 42.75) * mm});
            skLineSegment(sketch, "E12.18.25.0", {"start": v(66, 38.1) * mm, "end": v(62.38, 35.76) * mm});
            skLineSegment(sketch, "E12.21.25.0", {"start": v(61.65, 44.79) * mm, "end": v(57.98, 42.4) * mm});
            skArc(sketch, "E12.24.25.0", {"start": v(56.96, 42.6) * mm, "mid": v(57.43, 42.3) * mm, "end": v(57.98, 42.4) * mm});
            skArc(sketch, "E12.28.25.0", {"start": v(62.38, 35.76) * mm, "mid": v(62.03, 35.26) * mm, "end": v(62.1, 34.65) * mm});
            skArc(sketch, "E12.32.25.0", {"start": v(61.65, 44.79) * mm, "mid": v(64.31, 45.3) * mm, "end": v(67.02, 45.42) * mm});
            skLineSegment(sketch, "E12.1.26.0", {"start": v(56.78, 58.16) * mm, "end": v(57.48, 57.48) * mm});
            skArc(sketch, "E12.3.26.0", {"start": v(56.78, 58.16) * mm, "mid": v(56.47, 58.34) * mm, "end": v(56.11, 58.36) * mm});
            skLineSegment(sketch, "E12.7.26.0", {"start": v(58.16, 56.78) * mm, "end": v(57.48, 57.48) * mm});
            skArc(sketch, "E12.10.26.0", {"start": v(58.36, 56.11) * mm, "mid": v(58.34, 56.47) * mm, "end": v(58.16, 56.78) * mm});
            skArc(sketch, "E12.14.26.0", {"start": v(56.63, 50.99) * mm, "mid": v(57.68, 53.49) * mm, "end": v(58.36, 56.11) * mm});
            skLineSegment(sketch, "E12.18.26.0", {"start": v(56.63, 50.99) * mm, "end": v(53.59, 47.95) * mm});
            skLineSegment(sketch, "E12.21.26.0", {"start": v(50.99, 56.63) * mm, "end": v(47.9, 53.54) * mm});
            skArc(sketch, "E12.24.26.0", {"start": v(46.86, 53.5) * mm, "mid": v(47.38, 53.31) * mm, "end": v(47.9, 53.54) * mm});
            skArc(sketch, "E12.28.26.0", {"start": v(53.59, 47.95) * mm, "mid": v(53.34, 47.38) * mm, "end": v(53.55, 46.8) * mm});
            skArc(sketch, "E12.32.26.0", {"start": v(50.99, 56.63) * mm, "mid": v(53.49, 57.68) * mm, "end": v(56.11, 58.36) * mm});
            skLineSegment(sketch, "E12.1.27.0", {"start": v(43.45, 68.7) * mm, "end": v(44.27, 68.18) * mm});
            skArc(sketch, "E12.3.27.0", {"start": v(43.45, 68.7) * mm, "mid": v(43.1, 68.8) * mm, "end": v(42.75, 68.75) * mm});
            skLineSegment(sketch, "E12.7.27.0", {"start": v(45.09, 67.63) * mm, "end": v(44.27, 68.18) * mm});
            skArc(sketch, "E12.10.27.0", {"start": v(45.42, 67.02) * mm, "mid": v(45.33, 67.37) * mm, "end": v(45.09, 67.63) * mm});
            skArc(sketch, "E12.14.27.0", {"start": v(44.79, 61.65) * mm, "mid": v(45.3, 64.31) * mm, "end": v(45.42, 67.02) * mm});
            skLineSegment(sketch, "E12.18.27.0", {"start": v(44.79, 61.65) * mm, "end": v(42.45, 58.04) * mm});
            skLineSegment(sketch, "E12.21.27.0", {"start": v(38.1, 66) * mm, "end": v(35.72, 62.33) * mm});
            skArc(sketch, "E12.24.27.0", {"start": v(34.7, 62.08) * mm, "mid": v(35.26, 62) * mm, "end": v(35.72, 62.33) * mm});
            skArc(sketch, "E12.28.27.0", {"start": v(42.45, 58.04) * mm, "mid": v(42.32, 57.44) * mm, "end": v(42.65, 56.92) * mm});
            skArc(sketch, "E12.32.27.0", {"start": v(38.1, 66) * mm, "mid": v(40.33, 67.54) * mm, "end": v(42.75, 68.75) * mm});
            skLineSegment(sketch, "E12.1.28.0", {"start": v(28.21, 76.23) * mm, "end": v(29.13, 75.9) * mm});
            skArc(sketch, "E12.3.28.0", {"start": v(28.21, 76.23) * mm, "mid": v(27.86, 76.27) * mm, "end": v(27.52, 76.14) * mm});
            skLineSegment(sketch, "E12.7.28.0", {"start": v(30.04, 75.53) * mm, "end": v(29.13, 75.9) * mm});
            skArc(sketch, "E12.10.28.0", {"start": v(30.5, 75) * mm, "mid": v(30.33, 75.32) * mm, "end": v(30.04, 75.53) * mm});
            skArc(sketch, "E12.14.28.0", {"start": v(31, 69.61) * mm, "mid": v(30.94, 72.32) * mm, "end": v(30.5, 75) * mm});
            skLineSegment(sketch, "E12.18.28.0", {"start": v(31, 69.61) * mm, "end": v(29.45, 65.6) * mm});
            skLineSegment(sketch, "E12.21.28.0", {"start": v(23.55, 72.47) * mm, "end": v(21.98, 68.4) * mm});
            skArc(sketch, "E12.24.28.0", {"start": v(21.04, 67.94) * mm, "mid": v(21.6, 67.98) * mm, "end": v(21.98, 68.4) * mm});
            skArc(sketch, "E12.28.28.0", {"start": v(29.45, 65.6) * mm, "mid": v(29.46, 64.98) * mm, "end": v(29.88, 64.54) * mm});
            skArc(sketch, "E12.32.28.0", {"start": v(23.55, 72.47) * mm, "mid": v(25.4, 74.45) * mm, "end": v(27.52, 76.14) * mm});
            skLineSegment(sketch, "E12.1.29.0", {"start": v(11.75, 80.43) * mm, "end": v(12.72, 80.3) * mm});
            skArc(sketch, "E12.3.29.0", {"start": v(11.75, 80.43) * mm, "mid": v(11.4, 80.4) * mm, "end": v(11.09, 80.2) * mm});
            skLineSegment(sketch, "E12.7.29.0", {"start": v(13.68, 80.12) * mm, "end": v(12.72, 80.3) * mm});
            skArc(sketch, "E12.10.29.0", {"start": v(14.24, 79.7) * mm, "mid": v(14, 79.98) * mm, "end": v(13.68, 80.12) * mm});
            skArc(sketch, "E12.14.29.0", {"start": v(15.84, 74.53) * mm, "mid": v(15.22, 77.17) * mm, "end": v(14.24, 79.7) * mm});
            skLineSegment(sketch, "E12.18.29.0", {"start": v(15.84, 74.53) * mm, "end": v(15.17, 70.29) * mm});
            skLineSegment(sketch, "E12.21.29.0", {"start": v(7.97, 75.78) * mm, "end": v(7.28, 71.47) * mm});
            skArc(sketch, "E12.24.29.0", {"start": v(6.46, 70.83) * mm, "mid": v(7, 70.98) * mm, "end": v(7.28, 71.47) * mm});
            skArc(sketch, "E12.28.29.0", {"start": v(15.17, 70.29) * mm, "mid": v(15.3, 69.69) * mm, "end": v(15.8, 69.34) * mm});
            skArc(sketch, "E12.32.29.0", {"start": v(7.97, 75.78) * mm, "mid": v(9.37, 78.1) * mm, "end": v(11.09, 80.2) * mm});
            skArc(sketch, "E13.trimOffspring", {"start": v(-22.9, 67.33) * mm, "mid": v(-25.46, 66.4) * mm, "end": v(-27.97, 65.4) * mm});
            skArc(sketch, "E14.trimOffspring", {"start": v(-36.4, 61.1) * mm, "mid": v(-38.7, 59.66) * mm, "end": v(-40.95, 58.15) * mm});
            skArc(sketch, "E15.trimOffspring", {"start": v(-48.31, 52.2) * mm, "mid": v(-50.27, 50.31) * mm, "end": v(-52.15, 48.36) * mm});
            skArc(sketch, "E16.trimOffspring", {"start": v(-58.1, 41) * mm, "mid": v(-59.63, 38.76) * mm, "end": v(-61.06, 36.46) * mm});
            skArc(sketch, "E17.trimOffspring", {"start": v(-65.36, 28.03) * mm, "mid": v(-66.38, 25.52) * mm, "end": v(-67.3, 22.97) * mm});
            skArc(sketch, "E18.trimOffspring", {"start": v(-69.76, 13.83) * mm, "mid": v(-70.24, 11.16) * mm, "end": v(-70.61, 8.48) * mm});
            skArc(sketch, "E19.trimOffspring", {"start": v(-71.11, -0.98) * mm, "mid": v(-71.02, -3.69) * mm, "end": v(-70.83, -6.4) * mm});
            skArc(sketch, "E20.trimOffspring", {"start": v(-69.36, -15.74) * mm, "mid": v(-68.7, -18.37) * mm, "end": v(-67.96, -20.98) * mm});
            skArc(sketch, "E21.trimOffspring", {"start": v(-64.57, -29.82) * mm, "mid": v(-63.38, -32.26) * mm, "end": v(-62.1, -34.65) * mm});
            skArc(sketch, "E22.trimOffspring", {"start": v(-56.96, -42.6) * mm, "mid": v(-55.3, -44.73) * mm, "end": v(-53.55, -46.8) * mm});
            skArc(sketch, "E23.trimOffspring", {"start": v(-46.86, -53.5) * mm, "mid": v(-44.78, -55.25) * mm, "end": v(-42.65, -56.92) * mm});
            skArc(sketch, "E24.trimOffspring", {"start": v(-34.7, -62.08) * mm, "mid": v(-32.32, -63.35) * mm, "end": v(-29.88, -64.54) * mm});
            skArc(sketch, "E25.trimOffspring", {"start": v(-21.04, -67.94) * mm, "mid": v(-18.44, -68.69) * mm, "end": v(-15.8, -69.34) * mm});
            skArc(sketch, "E26.trimOffspring", {"start": v(-6.46, -70.83) * mm, "mid": v(-3.76, -71.02) * mm, "end": v(-1.05, -71.11) * mm});
            skArc(sketch, "E27.trimOffspring", {"start": v(8.4, -70.62) * mm, "mid": v(11.1, -70.25) * mm, "end": v(13.76, -69.78) * mm});
            skArc(sketch, "E28.trimOffspring", {"start": v(22.9, -67.33) * mm, "mid": v(25.46, -66.4) * mm, "end": v(27.97, -65.4) * mm});
            skArc(sketch, "E29.trimOffspring", {"start": v(36.4, -61.1) * mm, "mid": v(38.7, -59.66) * mm, "end": v(40.95, -58.15) * mm});
            skArc(sketch, "E30.trimOffspring", {"start": v(48.31, -52.2) * mm, "mid": v(50.27, -50.31) * mm, "end": v(52.15, -48.36) * mm});
            skArc(sketch, "E31.trimOffspring", {"start": v(58.1, -41) * mm, "mid": v(59.63, -38.76) * mm, "end": v(61.06, -36.46) * mm});
            skArc(sketch, "E32.trimOffspring", {"start": v(65.36, -28.03) * mm, "mid": v(66.38, -25.52) * mm, "end": v(67.3, -22.97) * mm});
            skArc(sketch, "E33.trimOffspring", {"start": v(69.76, -13.83) * mm, "mid": v(70.24, -11.16) * mm, "end": v(70.61, -8.48) * mm});
            skArc(sketch, "E34.trimOffspring", {"start": v(71.11, 0.98) * mm, "mid": v(71.02, 3.69) * mm, "end": v(70.83, 6.4) * mm});
            skArc(sketch, "E35.trimOffspring", {"start": v(69.36, 15.74) * mm, "mid": v(68.7, 18.37) * mm, "end": v(67.96, 20.98) * mm});
            skArc(sketch, "E36.trimOffspring", {"start": v(64.57, 29.82) * mm, "mid": v(63.38, 32.26) * mm, "end": v(62.1, 34.65) * mm});
            skArc(sketch, "E37.trimOffspring", {"start": v(56.96, 42.6) * mm, "mid": v(55.3, 44.73) * mm, "end": v(53.55, 46.8) * mm});
            skArc(sketch, "E38.trimOffspring", {"start": v(46.86, 53.5) * mm, "mid": v(44.78, 55.25) * mm, "end": v(42.65, 56.92) * mm});
            skArc(sketch, "E39.trimOffspring", {"start": v(34.7, 62.08) * mm, "mid": v(32.32, 63.35) * mm, "end": v(29.88, 64.54) * mm});
            skArc(sketch, "E40.trimOffspring", {"start": v(21.04, 67.94) * mm, "mid": v(18.44, 68.69) * mm, "end": v(15.8, 69.34) * mm});
            skArc(sketch, "E41.trimOffspring", {"start": v(6.46, 70.83) * mm, "mid": v(3.76, 71.02) * mm, "end": v(1.05, 71.11) * mm});
            skArc(sketch, "E42", {"start": v(-4.86, 65.4) * mm, "mid": v(-6.2, 65.29) * mm, "end": v(-7.54, 65.15) * mm});
            skLineSegment(sketch, "E43.MirrorCS", {"start": v(-3.99, 62.92) * mm, "end": v(-4.04, 64.67) * mm});
            skArc(sketch, "E44.MirrorCS", {"start": v(-3.99, 62.92) * mm, "mid": v(-3.52, 61.84) * mm, "end": v(-2.98, 60.8) * mm});
            skLineSegment(sketch, "E45.MirrorCS", {"start": v(-2.3, 60.41) * mm, "end": v(-1.9, 60.42) * mm});
            skLineSegment(sketch, "E46.MirrorCS", {"start": v(-1.5, 60.44) * mm, "end": v(-1.9, 60.42) * mm});
            skArc(sketch, "E47.MirrorCS", {"start": v(0.03, 63.05) * mm, "mid": v(-0.37, 61.94) * mm, "end": v(-0.84, 60.86) * mm});
            skLineSegment(sketch, "E48.MirrorCS", {"start": v(0.03, 63.05) * mm, "end": v(-0.03, 64.8) * mm});
            skPoint(sketch, "E49.visualSharp", {"position": v(-4.07, 65.46) * mm});
            skArc(sketch, "E49.filletArc", {"start": v(-4.04, 64.67) * mm, "mid": v(-4.3, 65.2) * mm, "end": v(-4.86, 65.4) * mm});
            skPoint(sketch, "E50.visualSharp", {"position": v(-0.05, 65.58) * mm});
            skArc(sketch, "E50.filletArc", {"start": v(0.74, 65.58) * mm, "mid": v(0.2, 65.35) * mm, "end": v(-0.03, 64.8) * mm});
            skPoint(sketch, "E51.visualSharp", {"position": v(-1.05, 60.45) * mm});
            skArc(sketch, "E51.filletArc", {"start": v(-1.5, 60.44) * mm, "mid": v(-1.11, 60.56) * mm, "end": v(-0.84, 60.86) * mm});
            skPoint(sketch, "E52.visualSharp", {"position": v(-2.75, 60.4) * mm});
            skArc(sketch, "E52.filletArc", {"start": v(-2.98, 60.8) * mm, "mid": v(-2.7, 60.5) * mm, "end": v(-2.3, 60.41) * mm});
            skArc(sketch, "E53.1.0", {"start": v(-12.17, 63.64) * mm, "mid": v(-12.49, 64.15) * mm, "end": v(-13.08, 64.27) * mm});
            skLineSegment(sketch, "E53.1.1", {"start": v(-11.9, 61.92) * mm, "end": v(-12.17, 63.64) * mm});
            skArc(sketch, "E53.1.2", {"start": v(-11.9, 61.92) * mm, "mid": v(-11.3, 60.9) * mm, "end": v(-10.64, 59.94) * mm});
            skArc(sketch, "E53.1.3", {"start": v(-10.64, 59.94) * mm, "mid": v(-10.31, 59.69) * mm, "end": v(-9.9, 59.64) * mm});
            skLineSegment(sketch, "E53.1.4", {"start": v(-9.9, 59.64) * mm, "end": v(-9.51, 59.7) * mm});
            skLineSegment(sketch, "E53.1.5", {"start": v(-9.12, 59.76) * mm, "end": v(-9.51, 59.7) * mm});
            skArc(sketch, "E53.1.6", {"start": v(-9.12, 59.76) * mm, "mid": v(-8.75, 59.93) * mm, "end": v(-8.52, 60.27) * mm});
            skArc(sketch, "E53.1.7", {"start": v(-7.93, 62.55) * mm, "mid": v(-8.18, 61.4) * mm, "end": v(-8.52, 60.27) * mm});
            skLineSegment(sketch, "E53.1.8", {"start": v(-7.93, 62.55) * mm, "end": v(-8.2, 64.27) * mm});
            skArc(sketch, "E53.1.9", {"start": v(-7.54, 65.15) * mm, "mid": v(-8.06, 64.85) * mm, "end": v(-8.2, 64.27) * mm});
            skArc(sketch, "E53.2.0", {"start": v(-20.1, 61.61) * mm, "mid": v(-20.49, 62.07) * mm, "end": v(-21.09, 62.12) * mm});
            skLineSegment(sketch, "E53.2.1", {"start": v(-19.62, 59.94) * mm, "end": v(-20.1, 61.61) * mm});
            skArc(sketch, "E53.2.2", {"start": v(-19.62, 59.94) * mm, "mid": v(-18.9, 59) * mm, "end": v(-18.12, 58.13) * mm});
            skArc(sketch, "E53.2.3", {"start": v(-18.12, 58.13) * mm, "mid": v(-17.77, 57.92) * mm, "end": v(-17.36, 57.92) * mm});
            skLineSegment(sketch, "E53.2.4", {"start": v(-17.36, 57.92) * mm, "end": v(-16.98, 58.03) * mm});
            skLineSegment(sketch, "E53.2.5", {"start": v(-16.6, 58.14) * mm, "end": v(-16.98, 58.03) * mm});
            skArc(sketch, "E53.2.6", {"start": v(-16.6, 58.14) * mm, "mid": v(-16.25, 58.36) * mm, "end": v(-16.06, 58.72) * mm});
            skArc(sketch, "E53.2.7", {"start": v(-15.77, 61.06) * mm, "mid": v(-15.87, 59.89) * mm, "end": v(-16.06, 58.72) * mm});
            skLineSegment(sketch, "E53.2.8", {"start": v(-15.77, 61.06) * mm, "end": v(-16.25, 62.73) * mm});
            skArc(sketch, "E53.2.9", {"start": v(-15.7, 63.69) * mm, "mid": v(-16.18, 63.33) * mm, "end": v(-16.25, 62.73) * mm});
            skArc(sketch, "E54.1.3.0", {"start": v(-27.73, 58.6) * mm, "mid": v(-28.16, 59.01) * mm, "end": v(-28.76, 58.98) * mm});
            skLineSegment(sketch, "E54.4.3.0", {"start": v(-27.04, 57) * mm, "end": v(-27.73, 58.6) * mm});
            skArc(sketch, "E54.7.3.0", {"start": v(-27.04, 57) * mm, "mid": v(-26.2, 56.16) * mm, "end": v(-25.32, 55.4) * mm});
            skArc(sketch, "E54.11.3.0", {"start": v(-25.32, 55.4) * mm, "mid": v(-24.94, 55.23) * mm, "end": v(-24.54, 55.29) * mm});
            skLineSegment(sketch, "E54.15.3.0", {"start": v(-24.54, 55.29) * mm, "end": v(-24.18, 55.44) * mm});
            skLineSegment(sketch, "E54.18.3.0", {"start": v(-23.81, 55.6) * mm, "end": v(-24.18, 55.44) * mm});
            skArc(sketch, "E54.21.3.0", {"start": v(-23.81, 55.6) * mm, "mid": v(-23.5, 55.86) * mm, "end": v(-23.35, 56.24) * mm});
            skArc(sketch, "E54.25.3.0", {"start": v(-23.35, 58.6) * mm, "mid": v(-23.3, 57.42) * mm, "end": v(-23.35, 56.24) * mm});
            skLineSegment(sketch, "E54.29.3.0", {"start": v(-23.35, 58.6) * mm, "end": v(-24.04, 60.2) * mm});
            skArc(sketch, "E54.32.3.0", {"start": v(-23.62, 61.2) * mm, "mid": v(-24.05, 60.8) * mm, "end": v(-24.04, 60.2) * mm});
            skArc(sketch, "E54.1.4.0", {"start": v(-34.91, 54.66) * mm, "mid": v(-35.4, 55.01) * mm, "end": v(-35.98, 54.9) * mm});
            skLineSegment(sketch, "E54.4.4.0", {"start": v(-34.03, 53.16) * mm, "end": v(-34.91, 54.66) * mm});
            skArc(sketch, "E54.7.4.0", {"start": v(-34.03, 53.16) * mm, "mid": v(-33.1, 52.43) * mm, "end": v(-32.12, 51.78) * mm});
            skArc(sketch, "E54.11.4.0", {"start": v(-32.12, 51.78) * mm, "mid": v(-31.73, 51.66) * mm, "end": v(-31.33, 51.77) * mm});
            skLineSegment(sketch, "E54.15.4.0", {"start": v(-31.33, 51.77) * mm, "end": v(-31, 51.97) * mm});
            skLineSegment(sketch, "E54.18.4.0", {"start": v(-30.65, 52.17) * mm, "end": v(-31, 51.97) * mm});
            skArc(sketch, "E54.21.4.0", {"start": v(-30.65, 52.17) * mm, "mid": v(-30.37, 52.47) * mm, "end": v(-30.28, 52.87) * mm});
            skArc(sketch, "E54.25.4.0", {"start": v(-30.57, 55.2) * mm, "mid": v(-30.38, 54.04) * mm, "end": v(-30.28, 52.87) * mm});
            skLineSegment(sketch, "E54.29.4.0", {"start": v(-30.57, 55.2) * mm, "end": v(-31.46, 56.7) * mm});
            skArc(sketch, "E54.32.4.0", {"start": v(-31.16, 57.76) * mm, "mid": v(-31.53, 57.3) * mm, "end": v(-31.46, 56.7) * mm});
            skArc(sketch, "E54.1.5.0", {"start": v(-41.55, 49.85) * mm, "mid": v(-42.07, 50.14) * mm, "end": v(-42.64, 49.96) * mm});
            skLineSegment(sketch, "E54.4.5.0", {"start": v(-40.48, 48.47) * mm, "end": v(-41.55, 49.85) * mm});
            skArc(sketch, "E54.7.5.0", {"start": v(-40.48, 48.47) * mm, "mid": v(-39.47, 47.86) * mm, "end": v(-38.41, 47.34) * mm});
            skArc(sketch, "E54.11.5.0", {"start": v(-38.41, 47.34) * mm, "mid": v(-38, 47.27) * mm, "end": v(-37.63, 47.43) * mm});
            skLineSegment(sketch, "E54.15.5.0", {"start": v(-37.63, 47.43) * mm, "end": v(-37.32, 47.67) * mm});
            skLineSegment(sketch, "E54.18.5.0", {"start": v(-37, 47.91) * mm, "end": v(-37.32, 47.67) * mm});
            skArc(sketch, "E54.21.5.0", {"start": v(-37, 47.91) * mm, "mid": v(-36.76, 48.24) * mm, "end": v(-36.72, 48.65) * mm});
            skArc(sketch, "E54.25.5.0", {"start": v(-37.3, 50.93) * mm, "mid": v(-36.97, 49.8) * mm, "end": v(-36.72, 48.65) * mm});
            skLineSegment(sketch, "E54.29.5.0", {"start": v(-37.3, 50.93) * mm, "end": v(-38.37, 52.3) * mm});
            skArc(sketch, "E54.32.5.0", {"start": v(-38.21, 53.4) * mm, "mid": v(-38.52, 52.89) * mm, "end": v(-38.37, 52.3) * mm});
            skArc(sketch, "E54.1.6.0", {"start": v(-47.52, 44.24) * mm, "mid": v(-48.08, 44.46) * mm, "end": v(-48.62, 44.22) * mm});
            skLineSegment(sketch, "E54.4.6.0", {"start": v(-46.3, 43) * mm, "end": v(-47.52, 44.24) * mm});
            skArc(sketch, "E54.7.6.0", {"start": v(-46.3, 43) * mm, "mid": v(-45.21, 42.53) * mm, "end": v(-44.1, 42.14) * mm});
            skArc(sketch, "E54.11.6.0", {"start": v(-44.1, 42.14) * mm, "mid": v(-43.7, 42.13) * mm, "end": v(-43.34, 42.33) * mm});
            skLineSegment(sketch, "E54.15.6.0", {"start": v(-43.34, 42.33) * mm, "end": v(-43.06, 42.61) * mm});
            skLineSegment(sketch, "E54.18.6.0", {"start": v(-42.78, 42.9) * mm, "end": v(-43.06, 42.61) * mm});
            skArc(sketch, "E54.21.6.0", {"start": v(-42.78, 42.9) * mm, "mid": v(-42.57, 43.25) * mm, "end": v(-42.59, 43.66) * mm});
            skArc(sketch, "E54.25.6.0", {"start": v(-43.45, 45.85) * mm, "mid": v(-42.98, 44.77) * mm, "end": v(-42.59, 43.66) * mm});
            skLineSegment(sketch, "E54.29.6.0", {"start": v(-43.45, 45.85) * mm, "end": v(-44.68, 47.08) * mm});
            skArc(sketch, "E54.32.6.0", {"start": v(-44.66, 48.18) * mm, "mid": v(-44.9, 47.63) * mm, "end": v(-44.68, 47.08) * mm});
            skArc(sketch, "E54.1.7.0", {"start": v(-52.75, 37.93) * mm, "mid": v(-53.33, 38.08) * mm, "end": v(-53.84, 37.77) * mm});
            skLineSegment(sketch, "E54.4.7.0", {"start": v(-51.37, 36.86) * mm, "end": v(-52.75, 37.93) * mm});
            skArc(sketch, "E54.7.7.0", {"start": v(-51.37, 36.86) * mm, "mid": v(-50.24, 36.53) * mm, "end": v(-49.1, 36.28) * mm});
            skArc(sketch, "E54.11.7.0", {"start": v(-49.1, 36.28) * mm, "mid": v(-48.69, 36.32) * mm, "end": v(-48.36, 36.56) * mm});
            skLineSegment(sketch, "E54.15.7.0", {"start": v(-48.36, 36.56) * mm, "end": v(-48.11, 36.87) * mm});
            skLineSegment(sketch, "E54.18.7.0", {"start": v(-47.87, 37.19) * mm, "end": v(-48.11, 36.87) * mm});
            skArc(sketch, "E54.21.7.0", {"start": v(-47.87, 37.19) * mm, "mid": v(-47.72, 37.57) * mm, "end": v(-47.78, 37.97) * mm});
            skArc(sketch, "E54.25.7.0", {"start": v(-48.91, 40.03) * mm, "mid": v(-48.3, 39.02) * mm, "end": v(-47.78, 37.97) * mm});
            skLineSegment(sketch, "E54.29.7.0", {"start": v(-48.91, 40.03) * mm, "end": v(-50.29, 41.1) * mm});
            skArc(sketch, "E54.32.7.0", {"start": v(-50.4, 42.2) * mm, "mid": v(-50.58, 41.63) * mm, "end": v(-50.29, 41.1) * mm});
            skArc(sketch, "E54.1.8.0", {"start": v(-57.14, 31.01) * mm, "mid": v(-57.74, 31.1) * mm, "end": v(-58.2, 30.72) * mm});
            skLineSegment(sketch, "E54.4.8.0", {"start": v(-55.64, 30.13) * mm, "end": v(-57.14, 31.01) * mm});
            skArc(sketch, "E54.7.8.0", {"start": v(-55.64, 30.13) * mm, "mid": v(-54.48, 29.94) * mm, "end": v(-53.3, 29.83) * mm});
            skArc(sketch, "E54.11.8.0", {"start": v(-53.3, 29.83) * mm, "mid": v(-52.91, 29.92) * mm, "end": v(-52.62, 30.2) * mm});
            skLineSegment(sketch, "E54.15.8.0", {"start": v(-52.62, 30.2) * mm, "end": v(-52.41, 30.55) * mm});
            skLineSegment(sketch, "E54.18.8.0", {"start": v(-52.21, 30.89) * mm, "end": v(-52.41, 30.55) * mm});
            skArc(sketch, "E54.21.8.0", {"start": v(-52.21, 30.89) * mm, "mid": v(-52.1, 31.28) * mm, "end": v(-52.22, 31.68) * mm});
            skArc(sketch, "E54.25.8.0", {"start": v(-53.6, 33.58) * mm, "mid": v(-52.87, 32.66) * mm, "end": v(-52.22, 31.68) * mm});
            skLineSegment(sketch, "E54.29.8.0", {"start": v(-53.6, 33.58) * mm, "end": v(-55.1, 34.47) * mm});
            skArc(sketch, "E54.32.8.0", {"start": v(-55.35, 35.54) * mm, "mid": v(-55.45, 34.95) * mm, "end": v(-55.1, 34.47) * mm});
            skArc(sketch, "E54.1.9.0", {"start": v(-60.64, 23.6) * mm, "mid": v(-61.24, 23.6) * mm, "end": v(-61.65, 23.17) * mm});
            skLineSegment(sketch, "E54.4.9.0", {"start": v(-59.04, 22.9) * mm, "end": v(-60.64, 23.6) * mm});
            skArc(sketch, "E54.7.9.0", {"start": v(-59.04, 22.9) * mm, "mid": v(-57.86, 22.87) * mm, "end": v(-56.69, 22.91) * mm});
            skArc(sketch, "E54.11.9.0", {"start": v(-56.69, 22.91) * mm, "mid": v(-56.3, 23.05) * mm, "end": v(-56.04, 23.37) * mm});
            skLineSegment(sketch, "E54.15.9.0", {"start": v(-56.04, 23.37) * mm, "end": v(-55.89, 23.73) * mm});
            skLineSegment(sketch, "E54.18.9.0", {"start": v(-55.73, 24.1) * mm, "end": v(-55.89, 23.73) * mm});
            skArc(sketch, "E54.21.9.0", {"start": v(-55.73, 24.1) * mm, "mid": v(-55.67, 24.5) * mm, "end": v(-55.83, 24.88) * mm});
            skArc(sketch, "E54.25.9.0", {"start": v(-57.44, 26.6) * mm, "mid": v(-56.6, 25.77) * mm, "end": v(-55.83, 24.88) * mm});
            skLineSegment(sketch, "E54.29.9.0", {"start": v(-57.44, 26.6) * mm, "end": v(-59.04, 27.29) * mm});
            skArc(sketch, "E54.32.9.0", {"start": v(-59.43, 28.32) * mm, "mid": v(-59.45, 27.72) * mm, "end": v(-59.04, 27.29) * mm});
            skArc(sketch, "E54.1.10.0", {"start": v(-63.18, 15.8) * mm, "mid": v(-63.77, 15.74) * mm, "end": v(-64.13, 15.26) * mm});
            skLineSegment(sketch, "E54.4.10.0", {"start": v(-61.5, 15.32) * mm, "end": v(-63.18, 15.8) * mm});
            skArc(sketch, "E54.7.10.0", {"start": v(-61.5, 15.32) * mm, "mid": v(-60.33, 15.43) * mm, "end": v(-59.17, 15.62) * mm});
            skArc(sketch, "E54.11.10.0", {"start": v(-59.17, 15.62) * mm, "mid": v(-58.8, 15.8) * mm, "end": v(-58.59, 16.16) * mm});
            skLineSegment(sketch, "E54.15.10.0", {"start": v(-58.59, 16.16) * mm, "end": v(-58.48, 16.54) * mm});
            skLineSegment(sketch, "E54.18.10.0", {"start": v(-58.37, 16.92) * mm, "end": v(-58.48, 16.54) * mm});
            skArc(sketch, "E54.21.10.0", {"start": v(-58.37, 16.92) * mm, "mid": v(-58.36, 17.33) * mm, "end": v(-58.57, 17.68) * mm});
            skArc(sketch, "E54.25.10.0", {"start": v(-60.38, 19.18) * mm, "mid": v(-59.45, 18.46) * mm, "end": v(-58.57, 17.68) * mm});
            skLineSegment(sketch, "E54.29.10.0", {"start": v(-60.38, 19.18) * mm, "end": v(-62.05, 19.67) * mm});
            skArc(sketch, "E54.32.10.0", {"start": v(-62.56, 20.64) * mm, "mid": v(-62.52, 20.05) * mm, "end": v(-62.05, 19.67) * mm});
            skArc(sketch, "E54.1.11.0", {"start": v(-64.72, 7.76) * mm, "mid": v(-65.3, 7.62) * mm, "end": v(-65.6, 7.1) * mm});
            skLineSegment(sketch, "E54.4.11.0", {"start": v(-63, 7.49) * mm, "end": v(-64.72, 7.76) * mm});
            skArc(sketch, "E54.7.11.0", {"start": v(-63, 7.49) * mm, "mid": v(-61.84, 7.74) * mm, "end": v(-60.72, 8.08) * mm});
            skArc(sketch, "E54.11.11.0", {"start": v(-60.72, 8.08) * mm, "mid": v(-60.38, 8.3) * mm, "end": v(-60.2, 8.68) * mm});
            skLineSegment(sketch, "E54.15.11.0", {"start": v(-60.2, 8.68) * mm, "end": v(-60.15, 9.07) * mm});
            skLineSegment(sketch, "E54.18.11.0", {"start": v(-60.08, 9.46) * mm, "end": v(-60.15, 9.07) * mm});
            skArc(sketch, "E54.21.11.0", {"start": v(-60.08, 9.46) * mm, "mid": v(-60.13, 9.87) * mm, "end": v(-60.38, 10.2) * mm});
            skArc(sketch, "E54.25.11.0", {"start": v(-62.37, 11.46) * mm, "mid": v(-61.35, 10.86) * mm, "end": v(-60.38, 10.2) * mm});
            skLineSegment(sketch, "E54.29.11.0", {"start": v(-62.37, 11.46) * mm, "end": v(-64.09, 11.73) * mm});
            skArc(sketch, "E54.32.11.0", {"start": v(-64.72, 12.63) * mm, "mid": v(-64.6, 12.05) * mm, "end": v(-64.09, 11.73) * mm});
            skArc(sketch, "E54.1.12.0", {"start": v(-65.24, -0.42) * mm, "mid": v(-65.8, -0.63) * mm, "end": v(-66.02, -1.19) * mm});
            skLineSegment(sketch, "E54.4.12.0", {"start": v(-63.5, -0.47) * mm, "end": v(-65.24, -0.42) * mm});
            skArc(sketch, "E54.7.12.0", {"start": v(-63.5, -0.47) * mm, "mid": v(-62.38, -0.08) * mm, "end": v(-61.3, 0.4) * mm});
            skArc(sketch, "E54.11.12.0", {"start": v(-61.3, 0.4) * mm, "mid": v(-61, 0.67) * mm, "end": v(-60.88, 1.06) * mm});
            skLineSegment(sketch, "E54.15.12.0", {"start": v(-60.88, 1.06) * mm, "end": v(-60.87, 1.46) * mm});
            skLineSegment(sketch, "E54.18.12.0", {"start": v(-60.85, 1.85) * mm, "end": v(-60.87, 1.46) * mm});
            skArc(sketch, "E54.21.12.0", {"start": v(-60.85, 1.85) * mm, "mid": v(-60.95, 2.25) * mm, "end": v(-61.24, 2.54) * mm});
            skArc(sketch, "E54.25.12.0", {"start": v(-63.37, 3.54) * mm, "mid": v(-62.28, 3.08) * mm, "end": v(-61.24, 2.54) * mm});
            skLineSegment(sketch, "E54.29.12.0", {"start": v(-63.37, 3.54) * mm, "end": v(-65.1, 3.6) * mm});
            skArc(sketch, "E54.32.12.0", {"start": v(-65.85, 4.42) * mm, "mid": v(-65.65, 3.85) * mm, "end": v(-65.1, 3.6) * mm});
            skArc(sketch, "E54.1.13.0", {"start": v(-64.73, -8.6) * mm, "mid": v(-65.25, -8.88) * mm, "end": v(-65.4, -9.46) * mm});
            skLineSegment(sketch, "E54.4.13.0", {"start": v(-63, -8.43) * mm, "end": v(-64.73, -8.6) * mm});
            skArc(sketch, "E54.7.13.0", {"start": v(-63, -8.43) * mm, "mid": v(-61.94, -7.9) * mm, "end": v(-60.93, -7.3) * mm});
            skArc(sketch, "E54.11.13.0", {"start": v(-60.93, -7.3) * mm, "mid": v(-60.66, -6.99) * mm, "end": v(-60.59, -6.58) * mm});
            skLineSegment(sketch, "E54.15.13.0", {"start": v(-60.59, -6.58) * mm, "end": v(-60.63, -6.19) * mm});
            skLineSegment(sketch, "E54.18.13.0", {"start": v(-60.66, -5.8) * mm, "end": v(-60.63, -6.19) * mm});
            skArc(sketch, "E54.21.13.0", {"start": v(-60.66, -5.8) * mm, "mid": v(-60.8, -5.41) * mm, "end": v(-61.13, -5.16) * mm});
            skArc(sketch, "E54.25.13.0", {"start": v(-63.37, -4.43) * mm, "mid": v(-62.24, -4.75) * mm, "end": v(-61.13, -5.16) * mm});
            skLineSegment(sketch, "E54.29.13.0", {"start": v(-63.37, -4.43) * mm, "end": v(-65.1, -4.6) * mm});
            skArc(sketch, "E54.32.13.0", {"start": v(-65.94, -3.88) * mm, "mid": v(-65.67, -4.41) * mm, "end": v(-65.1, -4.6) * mm});
            skArc(sketch, "E54.1.14.0", {"start": v(-63.2, -16.64) * mm, "mid": v(-63.68, -17) * mm, "end": v(-63.77, -17.59) * mm});
            skLineSegment(sketch, "E54.4.14.0", {"start": v(-61.5, -16.26) * mm, "end": v(-63.2, -16.64) * mm});
            skArc(sketch, "E54.7.14.0", {"start": v(-61.5, -16.26) * mm, "mid": v(-60.52, -15.6) * mm, "end": v(-59.6, -14.88) * mm});
            skArc(sketch, "E54.11.14.0", {"start": v(-59.6, -14.88) * mm, "mid": v(-59.36, -14.54) * mm, "end": v(-59.34, -14.13) * mm});
            skLineSegment(sketch, "E54.15.14.0", {"start": v(-59.34, -14.13) * mm, "end": v(-59.43, -13.74) * mm});
            skLineSegment(sketch, "E54.18.14.0", {"start": v(-59.52, -13.36) * mm, "end": v(-59.43, -13.74) * mm});
            skArc(sketch, "E54.21.14.0", {"start": v(-59.52, -13.36) * mm, "mid": v(-59.7, -13) * mm, "end": v(-60.06, -12.79) * mm});
            skArc(sketch, "E54.25.14.0", {"start": v(-62.37, -12.34) * mm, "mid": v(-61.2, -12.52) * mm, "end": v(-60.06, -12.79) * mm});
            skLineSegment(sketch, "E54.29.14.0", {"start": v(-62.37, -12.34) * mm, "end": v(-64.07, -12.72) * mm});
            skArc(sketch, "E54.32.14.0", {"start": v(-64.99, -12.12) * mm, "mid": v(-64.66, -12.62) * mm, "end": v(-64.07, -12.72) * mm});
            skArc(sketch, "E54.1.15.0", {"start": v(-60.67, -24.44) * mm, "mid": v(-61.1, -24.85) * mm, "end": v(-61.12, -25.44) * mm});
            skLineSegment(sketch, "E54.4.15.0", {"start": v(-59.03, -23.85) * mm, "end": v(-60.67, -24.44) * mm});
            skArc(sketch, "E54.7.15.0", {"start": v(-59.03, -23.85) * mm, "mid": v(-58.14, -23.07) * mm, "end": v(-57.32, -22.24) * mm});
            skArc(sketch, "E54.11.15.0", {"start": v(-57.32, -22.24) * mm, "mid": v(-57.13, -21.87) * mm, "end": v(-57.16, -21.46) * mm});
            skLineSegment(sketch, "E54.15.15.0", {"start": v(-57.16, -21.46) * mm, "end": v(-57.3, -21.09) * mm});
            skLineSegment(sketch, "E54.18.15.0", {"start": v(-57.43, -20.72) * mm, "end": v(-57.3, -21.09) * mm});
            skArc(sketch, "E54.21.15.0", {"start": v(-57.43, -20.72) * mm, "mid": v(-57.67, -20.38) * mm, "end": v(-58.04, -20.22) * mm});
            skArc(sketch, "E54.25.15.0", {"start": v(-60.39, -20.07) * mm, "mid": v(-59.21, -20.1) * mm, "end": v(-58.04, -20.22) * mm});
            skLineSegment(sketch, "E54.29.15.0", {"start": v(-60.39, -20.07) * mm, "end": v(-62.03, -20.66) * mm});
            skArc(sketch, "E54.32.15.0", {"start": v(-63.01, -20.17) * mm, "mid": v(-62.63, -20.63) * mm, "end": v(-62.03, -20.66) * mm});
            skArc(sketch, "E54.1.16.0", {"start": v(-57.18, -31.86) * mm, "mid": v(-57.57, -32.31) * mm, "end": v(-57.5, -32.9) * mm});
            skLineSegment(sketch, "E54.4.16.0", {"start": v(-55.63, -31.06) * mm, "end": v(-57.18, -31.86) * mm});
            skArc(sketch, "E54.7.16.0", {"start": v(-55.63, -31.06) * mm, "mid": v(-54.85, -30.18) * mm, "end": v(-54.13, -29.25) * mm});
            skArc(sketch, "E54.11.16.0", {"start": v(-54.13, -29.25) * mm, "mid": v(-54, -28.86) * mm, "end": v(-54.08, -28.46) * mm});
            skLineSegment(sketch, "E54.15.16.0", {"start": v(-54.08, -28.46) * mm, "end": v(-54.26, -28.1) * mm});
            skLineSegment(sketch, "E54.18.16.0", {"start": v(-54.44, -27.76) * mm, "end": v(-54.26, -28.1) * mm});
            skArc(sketch, "E54.21.16.0", {"start": v(-54.44, -27.76) * mm, "mid": v(-54.71, -27.46) * mm, "end": v(-55.1, -27.34) * mm});
            skArc(sketch, "E54.25.16.0", {"start": v(-57.46, -27.49) * mm, "mid": v(-56.28, -27.37) * mm, "end": v(-55.1, -27.34) * mm});
            skLineSegment(sketch, "E54.29.16.0", {"start": v(-57.46, -27.49) * mm, "end": v(-59, -28.28) * mm});
            skArc(sketch, "E54.32.16.0", {"start": v(-60.05, -27.91) * mm, "mid": v(-59.6, -28.32) * mm, "end": v(-59, -28.28) * mm});
            skArc(sketch, "E54.1.17.0", {"start": v(-52.8, -38.78) * mm, "mid": v(-53.12, -39.28) * mm, "end": v(-52.98, -39.86) * mm});
            skLineSegment(sketch, "E54.4.17.0", {"start": v(-51.36, -37.8) * mm, "end": v(-52.8, -38.78) * mm});
            skArc(sketch, "E54.7.17.0", {"start": v(-51.36, -37.8) * mm, "mid": v(-50.7, -36.83) * mm, "end": v(-50.1, -35.8) * mm});
            skArc(sketch, "E54.11.17.0", {"start": v(-50.1, -35.8) * mm, "mid": v(-50, -35.4) * mm, "end": v(-50.14, -35.02) * mm});
            skLineSegment(sketch, "E54.15.17.0", {"start": v(-50.14, -35.02) * mm, "end": v(-50.36, -34.7) * mm});
            skLineSegment(sketch, "E54.18.17.0", {"start": v(-50.59, -34.37) * mm, "end": v(-50.36, -34.7) * mm});
            skArc(sketch, "E54.21.17.0", {"start": v(-50.59, -34.37) * mm, "mid": v(-50.9, -34.1) * mm, "end": v(-51.3, -34.04) * mm});
            skArc(sketch, "E54.25.17.0", {"start": v(-53.61, -34.47) * mm, "mid": v(-52.47, -34.21) * mm, "end": v(-51.3, -34.04) * mm});
            skLineSegment(sketch, "E54.29.17.0", {"start": v(-53.61, -34.47) * mm, "end": v(-55.06, -35.45) * mm});
            skArc(sketch, "E54.32.17.0", {"start": v(-56.13, -35.23) * mm, "mid": v(-55.64, -35.57) * mm, "end": v(-55.06, -35.45) * mm});
            skArc(sketch, "E54.1.18.0", {"start": v(-47.58, -45.1) * mm, "mid": v(-47.84, -45.63) * mm, "end": v(-47.62, -46.2) * mm});
            skLineSegment(sketch, "E54.4.18.0", {"start": v(-46.27, -43.94) * mm, "end": v(-47.58, -45.1) * mm});
            skArc(sketch, "E54.7.18.0", {"start": v(-46.27, -43.94) * mm, "mid": v(-45.73, -42.9) * mm, "end": v(-45.27, -41.81) * mm});
            skArc(sketch, "E54.11.18.0", {"start": v(-45.27, -41.81) * mm, "mid": v(-45.23, -41.4) * mm, "end": v(-45.41, -41.03) * mm});
            skLineSegment(sketch, "E54.15.18.0", {"start": v(-45.41, -41.03) * mm, "end": v(-45.67, -40.74) * mm});
            skLineSegment(sketch, "E54.18.18.0", {"start": v(-45.94, -40.44) * mm, "end": v(-45.67, -40.74) * mm});
            skArc(sketch, "E54.21.18.0", {"start": v(-45.94, -40.44) * mm, "mid": v(-46.28, -40.22) * mm, "end": v(-46.69, -40.2) * mm});
            skArc(sketch, "E54.25.18.0", {"start": v(-48.93, -40.93) * mm, "mid": v(-47.82, -40.52) * mm, "end": v(-46.69, -40.2) * mm});
            skLineSegment(sketch, "E54.29.18.0", {"start": v(-48.93, -40.93) * mm, "end": v(-50.24, -42.08) * mm});
            skArc(sketch, "E54.32.18.0", {"start": v(-51.33, -41.99) * mm, "mid": v(-50.8, -42.27) * mm, "end": v(-50.24, -42.08) * mm});
            skArc(sketch, "E54.1.19.0", {"start": v(-41.6, -50.7) * mm, "mid": v(-41.8, -51.27) * mm, "end": v(-41.52, -51.8) * mm});
            skLineSegment(sketch, "E54.4.19.0", {"start": v(-40.46, -49.4) * mm, "end": v(-41.6, -50.7) * mm});
            skArc(sketch, "E54.7.19.0", {"start": v(-40.46, -49.4) * mm, "mid": v(-40.05, -48.3) * mm, "end": v(-39.73, -47.16) * mm});
            skArc(sketch, "E54.11.19.0", {"start": v(-39.73, -47.16) * mm, "mid": v(-39.75, -46.75) * mm, "end": v(-39.97, -46.4) * mm});
            skLineSegment(sketch, "E54.15.19.0", {"start": v(-39.97, -46.4) * mm, "end": v(-40.27, -46.15) * mm});
            skLineSegment(sketch, "E54.18.19.0", {"start": v(-40.56, -45.88) * mm, "end": v(-40.27, -46.15) * mm});
            skArc(sketch, "E54.21.19.0", {"start": v(-40.56, -45.88) * mm, "mid": v(-40.93, -45.7) * mm, "end": v(-41.34, -45.74) * mm});
            skArc(sketch, "E54.25.19.0", {"start": v(-43.47, -46.74) * mm, "mid": v(-42.42, -46.2) * mm, "end": v(-41.34, -45.74) * mm});
            skLineSegment(sketch, "E54.29.19.0", {"start": v(-43.47, -46.74) * mm, "end": v(-44.62, -48.05) * mm});
            skArc(sketch, "E54.32.19.0", {"start": v(-45.72, -48.1) * mm, "mid": v(-45.16, -48.3) * mm, "end": v(-44.62, -48.05) * mm});
            skArc(sketch, "E54.1.20.0", {"start": v(-34.98, -55.53) * mm, "mid": v(-35.1, -56.11) * mm, "end": v(-34.75, -56.6) * mm});
            skLineSegment(sketch, "E54.4.20.0", {"start": v(-34, -54.09) * mm, "end": v(-34.98, -55.53) * mm});
            skArc(sketch, "E54.7.20.0", {"start": v(-34, -54.09) * mm, "mid": v(-33.74, -52.94) * mm, "end": v(-33.57, -51.77) * mm});
            skArc(sketch, "E54.11.20.0", {"start": v(-33.57, -51.77) * mm, "mid": v(-33.63, -51.37) * mm, "end": v(-33.9, -51.06) * mm});
            skLineSegment(sketch, "E54.15.20.0", {"start": v(-33.9, -51.06) * mm, "end": v(-34.22, -50.83) * mm});
            skLineSegment(sketch, "E54.18.20.0", {"start": v(-34.55, -50.61) * mm, "end": v(-34.22, -50.83) * mm});
            skArc(sketch, "E54.21.20.0", {"start": v(-34.55, -50.61) * mm, "mid": v(-34.94, -50.48) * mm, "end": v(-35.34, -50.57) * mm});
            skArc(sketch, "E54.25.20.0", {"start": v(-37.33, -51.83) * mm, "mid": v(-36.35, -51.16) * mm, "end": v(-35.34, -50.57) * mm});
            skLineSegment(sketch, "E54.29.20.0", {"start": v(-37.33, -51.83) * mm, "end": v(-38.3, -53.27) * mm});
            skArc(sketch, "E54.32.20.0", {"start": v(-39.4, -53.45) * mm, "mid": v(-38.8, -53.6) * mm, "end": v(-38.3, -53.27) * mm});
            skArc(sketch, "E54.1.21.0", {"start": v(-27.8, -59.48) * mm, "mid": v(-27.85, -60.08) * mm, "end": v(-27.44, -60.52) * mm});
            skLineSegment(sketch, "E54.4.21.0", {"start": v(-27.01, -57.93) * mm, "end": v(-27.8, -59.48) * mm});
            skArc(sketch, "E54.7.21.0", {"start": v(-27.01, -57.93) * mm, "mid": v(-26.9, -56.75) * mm, "end": v(-26.87, -55.58) * mm});
            skArc(sketch, "E54.11.21.0", {"start": v(-26.87, -55.58) * mm, "mid": v(-26.98, -55.18) * mm, "end": v(-27.28, -54.9) * mm});
            skLineSegment(sketch, "E54.15.21.0", {"start": v(-27.28, -54.9) * mm, "end": v(-27.64, -54.73) * mm});
            skLineSegment(sketch, "E54.18.21.0", {"start": v(-28, -54.55) * mm, "end": v(-27.64, -54.73) * mm});
            skArc(sketch, "E54.21.21.0", {"start": v(-28, -54.55) * mm, "mid": v(-28.4, -54.47) * mm, "end": v(-28.78, -54.6) * mm});
            skArc(sketch, "E54.25.21.0", {"start": v(-30.6, -56.1) * mm, "mid": v(-29.71, -55.32) * mm, "end": v(-28.78, -54.6) * mm});
            skLineSegment(sketch, "E54.29.21.0", {"start": v(-30.6, -56.1) * mm, "end": v(-31.38, -57.66) * mm});
            skArc(sketch, "E54.32.21.0", {"start": v(-32.44, -57.97) * mm, "mid": v(-31.84, -58.04) * mm, "end": v(-31.38, -57.66) * mm});
            skArc(sketch, "E54.1.22.0", {"start": v(-20.19, -62.5) * mm, "mid": v(-20.15, -63.1) * mm, "end": v(-19.7, -63.49) * mm});
            skLineSegment(sketch, "E54.4.22.0", {"start": v(-19.6, -60.86) * mm, "end": v(-20.19, -62.5) * mm});
            skArc(sketch, "E54.7.22.0", {"start": v(-19.6, -60.86) * mm, "mid": v(-19.63, -59.68) * mm, "end": v(-19.75, -58.51) * mm});
            skArc(sketch, "E54.11.22.0", {"start": v(-19.75, -58.51) * mm, "mid": v(-19.91, -58.14) * mm, "end": v(-20.25, -57.9) * mm});
            skLineSegment(sketch, "E54.15.22.0", {"start": v(-20.25, -57.9) * mm, "end": v(-20.62, -57.77) * mm});
            skLineSegment(sketch, "E54.18.22.0", {"start": v(-21, -57.63) * mm, "end": v(-20.62, -57.77) * mm});
            skArc(sketch, "E54.21.22.0", {"start": v(-21, -57.63) * mm, "mid": v(-21.4, -57.6) * mm, "end": v(-21.76, -57.79) * mm});
            skArc(sketch, "E54.25.22.0", {"start": v(-23.38, -59.5) * mm, "mid": v(-22.6, -58.61) * mm, "end": v(-21.76, -57.79) * mm});
            skLineSegment(sketch, "E54.29.22.0", {"start": v(-23.38, -59.5) * mm, "end": v(-23.97, -61.14) * mm});
            skArc(sketch, "E54.32.22.0", {"start": v(-24.97, -61.59) * mm, "mid": v(-24.37, -61.58) * mm, "end": v(-23.97, -61.14) * mm});
            skArc(sketch, "E54.1.23.0", {"start": v(-12.25, -64.54) * mm, "mid": v(-12.14, -65.13) * mm, "end": v(-11.64, -65.46) * mm});
            skLineSegment(sketch, "E54.4.23.0", {"start": v(-11.87, -62.84) * mm, "end": v(-12.25, -64.54) * mm});
            skArc(sketch, "E54.7.23.0", {"start": v(-11.87, -62.84) * mm, "mid": v(-12.05, -61.68) * mm, "end": v(-12.32, -60.53) * mm});
            skArc(sketch, "E54.11.23.0", {"start": v(-12.32, -60.53) * mm, "mid": v(-12.53, -60.18) * mm, "end": v(-12.89, -59.99) * mm});
            skLineSegment(sketch, "E54.15.23.0", {"start": v(-12.89, -59.99) * mm, "end": v(-13.27, -59.9) * mm});
            skLineSegment(sketch, "E54.18.23.0", {"start": v(-13.66, -59.81) * mm, "end": v(-13.27, -59.9) * mm});
            skArc(sketch, "E54.21.23.0", {"start": v(-13.66, -59.81) * mm, "mid": v(-14.07, -59.83) * mm, "end": v(-14.4, -60.06) * mm});
            skArc(sketch, "E54.25.23.0", {"start": v(-15.8, -61.97) * mm, "mid": v(-15.13, -60.99) * mm, "end": v(-14.4, -60.06) * mm});
            skLineSegment(sketch, "E54.29.23.0", {"start": v(-15.8, -61.97) * mm, "end": v(-16.17, -63.67) * mm});
            skArc(sketch, "E54.32.23.0", {"start": v(-17.11, -64.24) * mm, "mid": v(-16.52, -64.15) * mm, "end": v(-16.17, -63.67) * mm});
            skArc(sketch, "E54.1.24.0", {"start": v(-4.12, -65.58) * mm, "mid": v(-3.94, -66.15) * mm, "end": v(-3.4, -66.4) * mm});
            skLineSegment(sketch, "E54.4.24.0", {"start": v(-3.96, -63.84) * mm, "end": v(-4.12, -65.58) * mm});
            skArc(sketch, "E54.7.24.0", {"start": v(-3.96, -63.84) * mm, "mid": v(-4.28, -62.7) * mm, "end": v(-4.69, -61.6) * mm});
            skArc(sketch, "E54.11.24.0", {"start": v(-4.69, -61.6) * mm, "mid": v(-4.94, -61.28) * mm, "end": v(-5.32, -61.13) * mm});
            skLineSegment(sketch, "E54.15.24.0", {"start": v(-5.32, -61.13) * mm, "end": v(-5.72, -61.1) * mm});
            skLineSegment(sketch, "E54.18.24.0", {"start": v(-6.11, -61.06) * mm, "end": v(-5.72, -61.1) * mm});
            skArc(sketch, "E54.21.24.0", {"start": v(-6.11, -61.06) * mm, "mid": v(-6.51, -61.13) * mm, "end": v(-6.82, -61.4) * mm});
            skArc(sketch, "E54.25.24.0", {"start": v(-7.96, -63.46) * mm, "mid": v(-7.43, -62.41) * mm, "end": v(-6.82, -61.4) * mm});
            skLineSegment(sketch, "E54.29.24.0", {"start": v(-7.96, -63.46) * mm, "end": v(-8.12, -65.2) * mm});
            skArc(sketch, "E54.32.24.0", {"start": v(-8.99, -65.88) * mm, "mid": v(-8.4, -65.72) * mm, "end": v(-8.12, -65.2) * mm});
            skArc(sketch, "E54.1.25.0", {"start": v(4.07, -65.58) * mm, "mid": v(4.32, -66.12) * mm, "end": v(4.89, -66.32) * mm});
            skLineSegment(sketch, "E54.4.25.0", {"start": v(4.02, -63.84) * mm, "end": v(4.07, -65.58) * mm});
            skArc(sketch, "E54.7.25.0", {"start": v(4.02, -63.84) * mm, "mid": v(3.55, -62.76) * mm, "end": v(3.01, -61.71) * mm});
            skArc(sketch, "E54.11.25.0", {"start": v(3.01, -61.71) * mm, "mid": v(2.72, -61.42) * mm, "end": v(2.32, -61.32) * mm});
            skLineSegment(sketch, "E54.15.25.0", {"start": v(2.32, -61.32) * mm, "end": v(1.93, -61.34) * mm});
            skLineSegment(sketch, "E54.18.25.0", {"start": v(1.53, -61.35) * mm, "end": v(1.93, -61.34) * mm});
            skArc(sketch, "E54.21.25.0", {"start": v(1.53, -61.35) * mm, "mid": v(1.14, -61.47) * mm, "end": v(0.87, -61.78) * mm});
            skArc(sketch, "E54.25.25.0", {"start": v(0, -63.97) * mm, "mid": v(0.4, -62.86) * mm, "end": v(0.87, -61.78) * mm});
            skLineSegment(sketch, "E54.29.25.0", {"start": v(0, -63.97) * mm, "end": v(0.06, -65.7) * mm});
            skArc(sketch, "E54.32.25.0", {"start": v(-0.71, -66.5) * mm, "mid": v(-0.16, -66.26) * mm, "end": v(0.06, -65.7) * mm});
            skArc(sketch, "E54.1.26.0", {"start": v(12.2, -64.56) * mm, "mid": v(12.52, -65.07) * mm, "end": v(13.1, -65.19) * mm});
            skLineSegment(sketch, "E54.4.26.0", {"start": v(11.93, -62.84) * mm, "end": v(12.2, -64.56) * mm});
            skArc(sketch, "E54.7.26.0", {"start": v(11.93, -62.84) * mm, "mid": v(11.33, -61.82) * mm, "end": v(10.66, -60.85) * mm});
            skArc(sketch, "E54.11.26.0", {"start": v(10.66, -60.85) * mm, "mid": v(10.34, -60.6) * mm, "end": v(9.93, -60.56) * mm});
            skLineSegment(sketch, "E54.15.26.0", {"start": v(9.93, -60.56) * mm, "end": v(9.54, -60.62) * mm});
            skLineSegment(sketch, "E54.18.26.0", {"start": v(9.15, -60.68) * mm, "end": v(9.54, -60.62) * mm});
            skArc(sketch, "E54.21.26.0", {"start": v(9.15, -60.68) * mm, "mid": v(8.78, -60.85) * mm, "end": v(8.55, -61.19) * mm});
            skArc(sketch, "E54.25.26.0", {"start": v(7.96, -63.47) * mm, "mid": v(8.21, -62.32) * mm, "end": v(8.55, -61.19) * mm});
            skLineSegment(sketch, "E54.29.26.0", {"start": v(7.96, -63.47) * mm, "end": v(8.23, -65.19) * mm});
            skArc(sketch, "E54.32.26.0", {"start": v(7.57, -66.06) * mm, "mid": v(8.09, -65.77) * mm, "end": v(8.23, -65.19) * mm});
            skArc(sketch, "E54.1.27.0", {"start": v(20.14, -62.53) * mm, "mid": v(20.52, -62.99) * mm, "end": v(21.11, -63.04) * mm});
            skLineSegment(sketch, "E54.4.27.0", {"start": v(19.65, -60.85) * mm, "end": v(20.14, -62.53) * mm});
            skArc(sketch, "E54.7.27.0", {"start": v(19.65, -60.85) * mm, "mid": v(18.93, -59.92) * mm, "end": v(18.15, -59.04) * mm});
            skArc(sketch, "E54.11.27.0", {"start": v(18.15, -59.04) * mm, "mid": v(17.8, -58.83) * mm, "end": v(17.39, -58.84) * mm});
            skLineSegment(sketch, "E54.15.27.0", {"start": v(17.39, -58.84) * mm, "end": v(17, -58.95) * mm});
            skLineSegment(sketch, "E54.18.27.0", {"start": v(16.63, -59.06) * mm, "end": v(17, -58.95) * mm});
            skArc(sketch, "E54.21.27.0", {"start": v(16.63, -59.06) * mm, "mid": v(16.28, -59.27) * mm, "end": v(16.1, -59.64) * mm});
            skArc(sketch, "E54.25.27.0", {"start": v(15.8, -61.97) * mm, "mid": v(15.9, -60.8) * mm, "end": v(16.1, -59.64) * mm});
            skLineSegment(sketch, "E54.29.27.0", {"start": v(15.8, -61.97) * mm, "end": v(16.28, -63.65) * mm});
            skArc(sketch, "E54.32.27.0", {"start": v(15.73, -64.6) * mm, "mid": v(16.2, -64.24) * mm, "end": v(16.28, -63.65) * mm});
            skArc(sketch, "E54.1.28.0", {"start": v(27.76, -59.51) * mm, "mid": v(28.2, -59.93) * mm, "end": v(28.8, -59.9) * mm});
            skLineSegment(sketch, "E54.4.28.0", {"start": v(27.07, -57.92) * mm, "end": v(27.76, -59.51) * mm});
            skArc(sketch, "E54.7.28.0", {"start": v(27.07, -57.92) * mm, "mid": v(26.24, -57.08) * mm, "end": v(25.35, -56.3) * mm});
            skArc(sketch, "E54.11.28.0", {"start": v(25.35, -56.3) * mm, "mid": v(24.97, -56.14) * mm, "end": v(24.57, -56.2) * mm});
            skLineSegment(sketch, "E54.15.28.0", {"start": v(24.57, -56.2) * mm, "end": v(24.2, -56.36) * mm});
            skLineSegment(sketch, "E54.18.28.0", {"start": v(23.84, -56.51) * mm, "end": v(24.2, -56.36) * mm});
            skArc(sketch, "E54.21.28.0", {"start": v(23.84, -56.51) * mm, "mid": v(23.52, -56.77) * mm, "end": v(23.38, -57.16) * mm});
            skArc(sketch, "E54.25.28.0", {"start": v(23.38, -59.51) * mm, "mid": v(23.34, -58.33) * mm, "end": v(23.38, -57.16) * mm});
            skLineSegment(sketch, "E54.29.28.0", {"start": v(23.38, -59.51) * mm, "end": v(24.07, -61.1) * mm});
            skArc(sketch, "E54.32.28.0", {"start": v(23.65, -62.12) * mm, "mid": v(24.08, -61.7) * mm, "end": v(24.07, -61.1) * mm});
            skArc(sketch, "E54.1.29.0", {"start": v(34.94, -55.57) * mm, "mid": v(35.42, -55.93) * mm, "end": v(36.01, -55.82) * mm});
            skLineSegment(sketch, "E54.4.29.0", {"start": v(34.06, -54.07) * mm, "end": v(34.94, -55.57) * mm});
            skArc(sketch, "E54.7.29.0", {"start": v(34.06, -54.07) * mm, "mid": v(33.13, -53.35) * mm, "end": v(32.15, -52.7) * mm});
            skArc(sketch, "E54.11.29.0", {"start": v(32.15, -52.7) * mm, "mid": v(31.76, -52.58) * mm, "end": v(31.36, -52.68) * mm});
            skLineSegment(sketch, "E54.15.29.0", {"start": v(31.36, -52.68) * mm, "end": v(31.02, -52.88) * mm});
            skLineSegment(sketch, "E54.18.29.0", {"start": v(30.68, -53.09) * mm, "end": v(31.02, -52.88) * mm});
            skArc(sketch, "E54.21.29.0", {"start": v(30.68, -53.09) * mm, "mid": v(30.4, -53.38) * mm, "end": v(30.3, -53.78) * mm});
            skArc(sketch, "E54.25.29.0", {"start": v(30.6, -56.12) * mm, "mid": v(30.4, -54.95) * mm, "end": v(30.3, -53.78) * mm});
            skLineSegment(sketch, "E54.29.29.0", {"start": v(30.6, -56.12) * mm, "end": v(31.48, -57.62) * mm});
            skArc(sketch, "E54.32.29.0", {"start": v(31.19, -58.68) * mm, "mid": v(31.56, -58.2) * mm, "end": v(31.48, -57.62) * mm});
            skArc(sketch, "E54.1.30.0", {"start": v(41.57, -50.76) * mm, "mid": v(42.1, -51.05) * mm, "end": v(42.67, -50.87) * mm});
            skLineSegment(sketch, "E54.4.30.0", {"start": v(40.5, -49.38) * mm, "end": v(41.57, -50.76) * mm});
            skArc(sketch, "E54.7.30.0", {"start": v(40.5, -49.38) * mm, "mid": v(39.5, -48.78) * mm, "end": v(38.44, -48.25) * mm});
            skArc(sketch, "E54.11.30.0", {"start": v(38.44, -48.25) * mm, "mid": v(38.04, -48.19) * mm, "end": v(37.66, -48.34) * mm});
            skLineSegment(sketch, "E54.15.30.0", {"start": v(37.66, -48.34) * mm, "end": v(37.35, -48.59) * mm});
            skLineSegment(sketch, "E54.18.30.0", {"start": v(37.03, -48.83) * mm, "end": v(37.35, -48.59) * mm});
            skArc(sketch, "E54.21.30.0", {"start": v(37.03, -48.83) * mm, "mid": v(36.79, -49.16) * mm, "end": v(36.75, -49.56) * mm});
            skArc(sketch, "E54.25.30.0", {"start": v(37.33, -51.84) * mm, "mid": v(37, -50.71) * mm, "end": v(36.75, -49.56) * mm});
            skLineSegment(sketch, "E54.29.30.0", {"start": v(37.33, -51.84) * mm, "end": v(38.4, -53.22) * mm});
            skArc(sketch, "E54.32.30.0", {"start": v(38.24, -54.3) * mm, "mid": v(38.55, -53.8) * mm, "end": v(38.4, -53.22) * mm});
            skArc(sketch, "E54.1.31.0", {"start": v(47.55, -45.15) * mm, "mid": v(48.1, -45.38) * mm, "end": v(48.65, -45.13) * mm});
            skLineSegment(sketch, "E54.4.31.0", {"start": v(46.32, -43.92) * mm, "end": v(47.55, -45.15) * mm});
            skArc(sketch, "E54.7.31.0", {"start": v(46.32, -43.92) * mm, "mid": v(45.24, -43.45) * mm, "end": v(44.13, -43.06) * mm});
            skArc(sketch, "E54.11.31.0", {"start": v(44.13, -43.06) * mm, "mid": v(43.72, -43.05) * mm, "end": v(43.36, -43.25) * mm});
            skLineSegment(sketch, "E54.15.31.0", {"start": v(43.36, -43.25) * mm, "end": v(43.08, -43.53) * mm});
            skLineSegment(sketch, "E54.18.31.0", {"start": v(42.8, -43.8) * mm, "end": v(43.08, -43.53) * mm});
            skArc(sketch, "E54.21.31.0", {"start": v(42.8, -43.8) * mm, "mid": v(42.6, -44.16) * mm, "end": v(42.62, -44.57) * mm});
            skArc(sketch, "E54.25.31.0", {"start": v(43.48, -46.76) * mm, "mid": v(43, -45.68) * mm, "end": v(42.62, -44.57) * mm});
            skLineSegment(sketch, "E54.29.31.0", {"start": v(43.48, -46.76) * mm, "end": v(44.71, -48) * mm});
            skArc(sketch, "E54.32.31.0", {"start": v(44.69, -49.1) * mm, "mid": v(44.93, -48.55) * mm, "end": v(44.71, -48) * mm});
            skArc(sketch, "E54.1.32.0", {"start": v(52.78, -38.84) * mm, "mid": v(53.36, -39) * mm, "end": v(53.87, -38.68) * mm});
            skLineSegment(sketch, "E54.4.32.0", {"start": v(51.4, -37.78) * mm, "end": v(52.78, -38.84) * mm});
            skArc(sketch, "E54.7.32.0", {"start": v(51.4, -37.78) * mm, "mid": v(50.27, -37.44) * mm, "end": v(49.12, -37.2) * mm});
            skArc(sketch, "E54.11.32.0", {"start": v(49.12, -37.2) * mm, "mid": v(48.71, -37.23) * mm, "end": v(48.39, -37.48) * mm});
            skLineSegment(sketch, "E54.15.32.0", {"start": v(48.39, -37.48) * mm, "end": v(48.14, -37.79) * mm});
            skLineSegment(sketch, "E54.18.32.0", {"start": v(47.9, -38.1) * mm, "end": v(48.14, -37.79) * mm});
            skArc(sketch, "E54.21.32.0", {"start": v(47.9, -38.1) * mm, "mid": v(47.74, -38.48) * mm, "end": v(47.8, -38.89) * mm});
            skArc(sketch, "E54.25.32.0", {"start": v(48.94, -40.95) * mm, "mid": v(48.34, -39.94) * mm, "end": v(47.8, -38.89) * mm});
            skLineSegment(sketch, "E54.29.32.0", {"start": v(48.94, -40.95) * mm, "end": v(50.32, -42.02) * mm});
            skArc(sketch, "E54.32.32.0", {"start": v(50.43, -43.11) * mm, "mid": v(50.6, -42.54) * mm, "end": v(50.32, -42.02) * mm});
            skArc(sketch, "E54.1.33.0", {"start": v(57.17, -31.93) * mm, "mid": v(57.77, -32) * mm, "end": v(58.23, -31.63) * mm});
            skLineSegment(sketch, "E54.4.33.0", {"start": v(55.67, -31.04) * mm, "end": v(57.17, -31.93) * mm});
            skArc(sketch, "E54.7.33.0", {"start": v(55.67, -31.04) * mm, "mid": v(54.51, -30.85) * mm, "end": v(53.34, -30.75) * mm});
            skArc(sketch, "E54.11.33.0", {"start": v(53.34, -30.75) * mm, "mid": v(52.94, -30.84) * mm, "end": v(52.64, -31.12) * mm});
            skLineSegment(sketch, "E54.15.33.0", {"start": v(52.64, -31.12) * mm, "end": v(52.44, -31.46) * mm});
            skLineSegment(sketch, "E54.18.33.0", {"start": v(52.24, -31.8) * mm, "end": v(52.44, -31.46) * mm});
            skArc(sketch, "E54.21.33.0", {"start": v(52.24, -31.8) * mm, "mid": v(52.13, -32.2) * mm, "end": v(52.25, -32.6) * mm});
            skArc(sketch, "E54.25.33.0", {"start": v(53.63, -34.5) * mm, "mid": v(52.9, -33.57) * mm, "end": v(52.25, -32.6) * mm});
            skLineSegment(sketch, "E54.29.33.0", {"start": v(53.63, -34.5) * mm, "end": v(55.13, -35.39) * mm});
            skArc(sketch, "E54.32.33.0", {"start": v(55.38, -36.46) * mm, "mid": v(55.48, -35.87) * mm, "end": v(55.13, -35.39) * mm});
            skArc(sketch, "E54.1.34.0", {"start": v(60.67, -24.52) * mm, "mid": v(61.27, -24.52) * mm, "end": v(61.68, -24.09) * mm});
            skLineSegment(sketch, "E54.4.34.0", {"start": v(59.07, -23.82) * mm, "end": v(60.67, -24.52) * mm});
            skArc(sketch, "E54.7.34.0", {"start": v(59.07, -23.82) * mm, "mid": v(57.9, -23.78) * mm, "end": v(56.71, -23.83) * mm});
            skArc(sketch, "E54.11.34.0", {"start": v(56.71, -23.83) * mm, "mid": v(56.33, -23.97) * mm, "end": v(56.07, -24.28) * mm});
            skLineSegment(sketch, "E54.15.34.0", {"start": v(56.07, -24.28) * mm, "end": v(55.91, -24.65) * mm});
            skLineSegment(sketch, "E54.18.34.0", {"start": v(55.76, -25.01) * mm, "end": v(55.91, -24.65) * mm});
            skArc(sketch, "E54.21.34.0", {"start": v(55.76, -25.01) * mm, "mid": v(55.7, -25.42) * mm, "end": v(55.86, -25.8) * mm});
            skArc(sketch, "E54.25.34.0", {"start": v(57.47, -27.5) * mm, "mid": v(56.64, -26.68) * mm, "end": v(55.86, -25.8) * mm});
            skLineSegment(sketch, "E54.29.34.0", {"start": v(57.47, -27.5) * mm, "end": v(59.07, -28.2) * mm});
            skArc(sketch, "E54.32.34.0", {"start": v(59.46, -29.23) * mm, "mid": v(59.48, -28.64) * mm, "end": v(59.07, -28.2) * mm});
            skArc(sketch, "E54.1.35.0", {"start": v(63.2, -16.72) * mm, "mid": v(63.8, -16.65) * mm, "end": v(64.16, -16.17) * mm});
            skLineSegment(sketch, "E54.4.35.0", {"start": v(61.53, -16.24) * mm, "end": v(63.2, -16.72) * mm});
            skArc(sketch, "E54.7.35.0", {"start": v(61.53, -16.24) * mm, "mid": v(60.36, -16.34) * mm, "end": v(59.2, -16.54) * mm});
            skArc(sketch, "E54.11.35.0", {"start": v(59.2, -16.54) * mm, "mid": v(58.83, -16.72) * mm, "end": v(58.62, -17.07) * mm});
            skLineSegment(sketch, "E54.15.35.0", {"start": v(58.62, -17.07) * mm, "end": v(58.5, -17.45) * mm});
            skLineSegment(sketch, "E54.18.35.0", {"start": v(58.4, -17.83) * mm, "end": v(58.5, -17.45) * mm});
            skArc(sketch, "E54.21.35.0", {"start": v(58.4, -17.83) * mm, "mid": v(58.4, -18.24) * mm, "end": v(58.6, -18.6) * mm});
            skArc(sketch, "E54.25.35.0", {"start": v(60.4, -20.1) * mm, "mid": v(59.48, -19.38) * mm, "end": v(58.6, -18.6) * mm});
            skLineSegment(sketch, "E54.29.35.0", {"start": v(60.4, -20.1) * mm, "end": v(62.08, -20.58) * mm});
            skArc(sketch, "E54.32.35.0", {"start": v(62.6, -21.56) * mm, "mid": v(62.55, -20.96) * mm, "end": v(62.08, -20.58) * mm});
            skArc(sketch, "E54.1.36.0", {"start": v(64.74, -8.68) * mm, "mid": v(65.32, -8.53) * mm, "end": v(65.62, -8.01) * mm});
            skLineSegment(sketch, "E54.4.36.0", {"start": v(63.02, -8.4) * mm, "end": v(64.74, -8.68) * mm});
            skArc(sketch, "E54.7.36.0", {"start": v(63.02, -8.4) * mm, "mid": v(61.87, -8.66) * mm, "end": v(60.74, -9) * mm});
            skArc(sketch, "E54.11.36.0", {"start": v(60.74, -9) * mm, "mid": v(60.4, -9.22) * mm, "end": v(60.24, -9.6) * mm});
            skLineSegment(sketch, "E54.15.36.0", {"start": v(60.24, -9.6) * mm, "end": v(60.17, -9.99) * mm});
            skLineSegment(sketch, "E54.18.36.0", {"start": v(60.11, -10.38) * mm, "end": v(60.17, -9.99) * mm});
            skArc(sketch, "E54.21.36.0", {"start": v(60.11, -10.38) * mm, "mid": v(60.16, -10.78) * mm, "end": v(60.4, -11.1) * mm});
            skArc(sketch, "E54.25.36.0", {"start": v(62.4, -12.37) * mm, "mid": v(61.38, -11.78) * mm, "end": v(60.4, -11.1) * mm});
            skLineSegment(sketch, "E54.29.36.0", {"start": v(62.4, -12.37) * mm, "end": v(64.12, -12.64) * mm});
            skArc(sketch, "E54.32.36.0", {"start": v(64.74, -13.55) * mm, "mid": v(64.62, -12.96) * mm, "end": v(64.12, -12.64) * mm});
            skArc(sketch, "E54.1.37.0", {"start": v(65.26, -0.5) * mm, "mid": v(65.82, -0.28) * mm, "end": v(66.05, 0.27) * mm});
            skLineSegment(sketch, "E54.4.37.0", {"start": v(63.52, -0.44) * mm, "end": v(65.26, -0.5) * mm});
            skArc(sketch, "E54.7.37.0", {"start": v(63.52, -0.44) * mm, "mid": v(62.41, -0.84) * mm, "end": v(61.34, -1.31) * mm});
            skArc(sketch, "E54.11.37.0", {"start": v(61.34, -1.31) * mm, "mid": v(61.03, -1.58) * mm, "end": v(60.9, -1.97) * mm});
            skLineSegment(sketch, "E54.15.37.0", {"start": v(60.9, -1.97) * mm, "end": v(60.9, -2.37) * mm});
            skLineSegment(sketch, "E54.18.37.0", {"start": v(60.88, -2.77) * mm, "end": v(60.9, -2.37) * mm});
            skArc(sketch, "E54.21.37.0", {"start": v(60.88, -2.77) * mm, "mid": v(60.98, -3.16) * mm, "end": v(61.27, -3.45) * mm});
            skArc(sketch, "E54.25.37.0", {"start": v(63.4, -4.46) * mm, "mid": v(62.31, -4) * mm, "end": v(61.27, -3.45) * mm});
            skLineSegment(sketch, "E54.29.37.0", {"start": v(63.4, -4.46) * mm, "end": v(65.14, -4.51) * mm});
            skArc(sketch, "E54.32.37.0", {"start": v(65.87, -5.33) * mm, "mid": v(65.68, -4.77) * mm, "end": v(65.14, -4.51) * mm});
            skArc(sketch, "E54.1.38.0", {"start": v(64.76, 7.68) * mm, "mid": v(65.28, 7.97) * mm, "end": v(65.44, 8.54) * mm});
            skLineSegment(sketch, "E54.4.38.0", {"start": v(63.02, 7.52) * mm, "end": v(64.76, 7.68) * mm});
            skArc(sketch, "E54.7.38.0", {"start": v(63.02, 7.52) * mm, "mid": v(61.97, 6.99) * mm, "end": v(60.96, 6.38) * mm});
            skArc(sketch, "E54.11.38.0", {"start": v(60.96, 6.38) * mm, "mid": v(60.69, 6.07) * mm, "end": v(60.62, 5.67) * mm});
            skLineSegment(sketch, "E54.15.38.0", {"start": v(60.62, 5.67) * mm, "end": v(60.65, 5.27) * mm});
            skLineSegment(sketch, "E54.18.38.0", {"start": v(60.7, 4.88) * mm, "end": v(60.65, 5.27) * mm});
            skArc(sketch, "E54.21.38.0", {"start": v(60.7, 4.88) * mm, "mid": v(60.84, 4.5) * mm, "end": v(61.16, 4.25) * mm});
            skArc(sketch, "E54.25.38.0", {"start": v(63.4, 3.52) * mm, "mid": v(62.27, 3.84) * mm, "end": v(61.16, 4.25) * mm});
            skLineSegment(sketch, "E54.29.38.0", {"start": v(63.4, 3.52) * mm, "end": v(65.13, 3.68) * mm});
            skArc(sketch, "E54.32.38.0", {"start": v(65.97, 2.96) * mm, "mid": v(65.7, 3.5) * mm, "end": v(65.13, 3.68) * mm});
            skArc(sketch, "E54.1.39.0", {"start": v(63.22, 15.73) * mm, "mid": v(63.71, 16.08) * mm, "end": v(63.8, 16.67) * mm});
            skLineSegment(sketch, "E54.4.39.0", {"start": v(61.52, 15.35) * mm, "end": v(63.22, 15.73) * mm});
            skArc(sketch, "E54.7.39.0", {"start": v(61.52, 15.35) * mm, "mid": v(60.55, 14.7) * mm, "end": v(59.62, 13.96) * mm});
            skArc(sketch, "E54.11.39.0", {"start": v(59.62, 13.96) * mm, "mid": v(59.4, 13.63) * mm, "end": v(59.37, 13.22) * mm});
            skLineSegment(sketch, "E54.15.39.0", {"start": v(59.37, 13.22) * mm, "end": v(59.46, 12.83) * mm});
            skLineSegment(sketch, "E54.18.39.0", {"start": v(59.54, 12.44) * mm, "end": v(59.46, 12.83) * mm});
            skArc(sketch, "E54.21.39.0", {"start": v(59.54, 12.44) * mm, "mid": v(59.74, 12.08) * mm, "end": v(60.09, 11.87) * mm});
            skArc(sketch, "E54.25.39.0", {"start": v(62.4, 11.43) * mm, "mid": v(61.24, 11.6) * mm, "end": v(60.09, 11.87) * mm});
            skLineSegment(sketch, "E54.29.39.0", {"start": v(62.4, 11.43) * mm, "end": v(64.1, 11.8) * mm});
            skArc(sketch, "E54.32.39.0", {"start": v(65.02, 11.2) * mm, "mid": v(64.69, 11.7) * mm, "end": v(64.1, 11.8) * mm});
            skArc(sketch, "E54.1.40.0", {"start": v(60.7, 23.52) * mm, "mid": v(61.14, 23.93) * mm, "end": v(61.14, 24.53) * mm});
            skLineSegment(sketch, "E54.4.40.0", {"start": v(59.06, 22.93) * mm, "end": v(60.7, 23.52) * mm});
            skArc(sketch, "E54.7.40.0", {"start": v(59.06, 22.93) * mm, "mid": v(58.17, 22.16) * mm, "end": v(57.34, 21.32) * mm});
            skArc(sketch, "E54.11.40.0", {"start": v(57.34, 21.32) * mm, "mid": v(57.16, 20.96) * mm, "end": v(57.19, 20.55) * mm});
            skLineSegment(sketch, "E54.15.40.0", {"start": v(57.19, 20.55) * mm, "end": v(57.32, 20.18) * mm});
            skLineSegment(sketch, "E54.18.40.0", {"start": v(57.46, 19.8) * mm, "end": v(57.32, 20.18) * mm});
            skArc(sketch, "E54.21.40.0", {"start": v(57.46, 19.8) * mm, "mid": v(57.7, 19.47) * mm, "end": v(58.07, 19.3) * mm});
            skArc(sketch, "E54.25.40.0", {"start": v(60.42, 19.15) * mm, "mid": v(59.24, 19.19) * mm, "end": v(58.07, 19.3) * mm});
            skLineSegment(sketch, "E54.29.40.0", {"start": v(60.42, 19.15) * mm, "end": v(62.06, 19.75) * mm});
            skArc(sketch, "E54.32.40.0", {"start": v(63.04, 19.26) * mm, "mid": v(62.66, 19.71) * mm, "end": v(62.06, 19.75) * mm});
            skArc(sketch, "E54.1.41.0", {"start": v(57.21, 30.94) * mm, "mid": v(57.6, 31.4) * mm, "end": v(57.53, 32) * mm});
            skLineSegment(sketch, "E54.4.41.0", {"start": v(55.66, 30.15) * mm, "end": v(57.21, 30.94) * mm});
            skArc(sketch, "E54.7.41.0", {"start": v(55.66, 30.15) * mm, "mid": v(54.88, 29.27) * mm, "end": v(54.16, 28.33) * mm});
            skArc(sketch, "E54.11.41.0", {"start": v(54.16, 28.33) * mm, "mid": v(54.02, 27.95) * mm, "end": v(54.1, 27.55) * mm});
            skLineSegment(sketch, "E54.15.41.0", {"start": v(54.1, 27.55) * mm, "end": v(54.29, 27.2) * mm});
            skLineSegment(sketch, "E54.18.41.0", {"start": v(54.47, 26.84) * mm, "end": v(54.29, 27.2) * mm});
            skArc(sketch, "E54.21.41.0", {"start": v(54.47, 26.84) * mm, "mid": v(54.74, 26.54) * mm, "end": v(55.13, 26.43) * mm});
            skArc(sketch, "E54.25.41.0", {"start": v(57.48, 26.57) * mm, "mid": v(56.31, 26.45) * mm, "end": v(55.13, 26.43) * mm});
            skLineSegment(sketch, "E54.29.41.0", {"start": v(57.48, 26.57) * mm, "end": v(59.04, 27.36) * mm});
            skArc(sketch, "E54.32.41.0", {"start": v(60.08, 27) * mm, "mid": v(59.63, 27.4) * mm, "end": v(59.04, 27.36) * mm});
            skArc(sketch, "E54.1.42.0", {"start": v(52.83, 37.86) * mm, "mid": v(53.15, 38.37) * mm, "end": v(53.01, 38.95) * mm});
            skLineSegment(sketch, "E54.4.42.0", {"start": v(51.39, 36.88) * mm, "end": v(52.83, 37.86) * mm});
            skArc(sketch, "E54.7.42.0", {"start": v(51.39, 36.88) * mm, "mid": v(50.72, 35.91) * mm, "end": v(50.13, 34.9) * mm});
            skArc(sketch, "E54.11.42.0", {"start": v(50.13, 34.9) * mm, "mid": v(50.04, 34.5) * mm, "end": v(50.17, 34.1) * mm});
            skLineSegment(sketch, "E54.15.42.0", {"start": v(50.17, 34.1) * mm, "end": v(50.4, 33.78) * mm});
            skLineSegment(sketch, "E54.18.42.0", {"start": v(50.61, 33.45) * mm, "end": v(50.4, 33.78) * mm});
            skArc(sketch, "E54.21.42.0", {"start": v(50.61, 33.45) * mm, "mid": v(50.93, 33.19) * mm, "end": v(51.33, 33.12) * mm});
            skArc(sketch, "E54.25.42.0", {"start": v(53.64, 33.56) * mm, "mid": v(52.5, 33.3) * mm, "end": v(51.33, 33.12) * mm});
            skLineSegment(sketch, "E54.29.42.0", {"start": v(53.64, 33.56) * mm, "end": v(55.08, 34.54) * mm});
            skArc(sketch, "E54.32.42.0", {"start": v(56.16, 34.31) * mm, "mid": v(55.67, 34.66) * mm, "end": v(55.08, 34.54) * mm});
            skArc(sketch, "E54.1.43.0", {"start": v(47.6, 44.18) * mm, "mid": v(47.87, 44.72) * mm, "end": v(47.65, 45.28) * mm});
            skLineSegment(sketch, "E54.4.43.0", {"start": v(46.3, 43.03) * mm, "end": v(47.6, 44.18) * mm});
            skArc(sketch, "E54.7.43.0", {"start": v(46.3, 43.03) * mm, "mid": v(45.76, 41.98) * mm, "end": v(45.3, 40.9) * mm});
            skArc(sketch, "E54.11.43.0", {"start": v(45.3, 40.9) * mm, "mid": v(45.26, 40.49) * mm, "end": v(45.44, 40.12) * mm});
            skLineSegment(sketch, "E54.15.43.0", {"start": v(45.44, 40.12) * mm, "end": v(45.7, 39.82) * mm});
            skLineSegment(sketch, "E54.18.43.0", {"start": v(45.97, 39.53) * mm, "end": v(45.7, 39.82) * mm});
            skArc(sketch, "E54.21.43.0", {"start": v(45.97, 39.53) * mm, "mid": v(46.3, 39.3) * mm, "end": v(46.72, 39.29) * mm});
            skArc(sketch, "E54.25.43.0", {"start": v(48.96, 40.01) * mm, "mid": v(47.85, 39.61) * mm, "end": v(46.72, 39.29) * mm});
            skLineSegment(sketch, "E54.29.43.0", {"start": v(48.96, 40.01) * mm, "end": v(50.26, 41.17) * mm});
            skArc(sketch, "E54.32.43.0", {"start": v(51.36, 41.07) * mm, "mid": v(50.83, 41.35) * mm, "end": v(50.26, 41.17) * mm});
            skArc(sketch, "E54.1.44.0", {"start": v(41.64, 49.8) * mm, "mid": v(41.83, 50.36) * mm, "end": v(41.55, 50.89) * mm});
            skLineSegment(sketch, "E54.4.44.0", {"start": v(40.49, 48.49) * mm, "end": v(41.64, 49.8) * mm});
            skArc(sketch, "E54.7.44.0", {"start": v(40.49, 48.49) * mm, "mid": v(40.08, 47.38) * mm, "end": v(39.76, 46.25) * mm});
            skArc(sketch, "E54.11.44.0", {"start": v(39.76, 46.25) * mm, "mid": v(39.77, 45.84) * mm, "end": v(40, 45.5) * mm});
            skLineSegment(sketch, "E54.15.44.0", {"start": v(40, 45.5) * mm, "end": v(40.3, 45.23) * mm});
            skLineSegment(sketch, "E54.18.44.0", {"start": v(40.6, 44.97) * mm, "end": v(40.3, 45.23) * mm});
            skArc(sketch, "E54.21.44.0", {"start": v(40.6, 44.97) * mm, "mid": v(40.96, 44.8) * mm, "end": v(41.37, 44.83) * mm});
            skArc(sketch, "E54.25.44.0", {"start": v(43.5, 45.83) * mm, "mid": v(42.45, 45.29) * mm, "end": v(41.37, 44.83) * mm});
            skLineSegment(sketch, "E54.29.44.0", {"start": v(43.5, 45.83) * mm, "end": v(44.65, 47.14) * mm});
            skArc(sketch, "E54.32.44.0", {"start": v(45.75, 47.18) * mm, "mid": v(45.2, 47.4) * mm, "end": v(44.65, 47.14) * mm});
            skArc(sketch, "E54.1.45.0", {"start": v(35.01, 54.61) * mm, "mid": v(35.13, 55.2) * mm, "end": v(34.78, 55.69) * mm});
            skLineSegment(sketch, "E54.4.45.0", {"start": v(34.03, 53.17) * mm, "end": v(35.01, 54.61) * mm});
            skArc(sketch, "E54.7.45.0", {"start": v(34.03, 53.17) * mm, "mid": v(33.77, 52.02) * mm, "end": v(33.6, 50.86) * mm});
            skArc(sketch, "E54.11.45.0", {"start": v(33.6, 50.86) * mm, "mid": v(33.66, 50.46) * mm, "end": v(33.92, 50.14) * mm});
            skLineSegment(sketch, "E54.15.45.0", {"start": v(33.92, 50.14) * mm, "end": v(34.25, 49.92) * mm});
            skLineSegment(sketch, "E54.18.45.0", {"start": v(34.58, 49.7) * mm, "end": v(34.25, 49.92) * mm});
            skArc(sketch, "E54.21.45.0", {"start": v(34.58, 49.7) * mm, "mid": v(34.97, 49.57) * mm, "end": v(35.37, 49.66) * mm});
            skArc(sketch, "E54.25.45.0", {"start": v(37.35, 50.91) * mm, "mid": v(36.38, 50.25) * mm, "end": v(35.37, 49.66) * mm});
            skLineSegment(sketch, "E54.29.45.0", {"start": v(37.35, 50.91) * mm, "end": v(38.33, 52.36) * mm});
            skArc(sketch, "E54.32.45.0", {"start": v(39.42, 52.54) * mm, "mid": v(38.84, 52.68) * mm, "end": v(38.33, 52.36) * mm});
            skArc(sketch, "E54.1.46.0", {"start": v(27.83, 58.57) * mm, "mid": v(27.87, 59.16) * mm, "end": v(27.47, 59.6) * mm});
            skLineSegment(sketch, "E54.4.46.0", {"start": v(27.04, 57.01) * mm, "end": v(27.83, 58.57) * mm});
            skArc(sketch, "E54.7.46.0", {"start": v(27.04, 57.01) * mm, "mid": v(26.93, 55.84) * mm, "end": v(26.9, 54.66) * mm});
            skArc(sketch, "E54.11.46.0", {"start": v(26.9, 54.66) * mm, "mid": v(27.01, 54.27) * mm, "end": v(27.31, 54) * mm});
            skLineSegment(sketch, "E54.15.46.0", {"start": v(27.31, 54) * mm, "end": v(27.67, 53.81) * mm});
            skLineSegment(sketch, "E54.18.46.0", {"start": v(28.02, 53.63) * mm, "end": v(27.67, 53.81) * mm});
            skArc(sketch, "E54.21.46.0", {"start": v(28.02, 53.63) * mm, "mid": v(28.42, 53.55) * mm, "end": v(28.8, 53.7) * mm});
            skArc(sketch, "E54.25.46.0", {"start": v(30.62, 55.19) * mm, "mid": v(29.74, 54.4) * mm, "end": v(28.8, 53.7) * mm});
            skLineSegment(sketch, "E54.29.46.0", {"start": v(30.62, 55.19) * mm, "end": v(31.41, 56.74) * mm});
            skArc(sketch, "E54.32.46.0", {"start": v(32.47, 57.06) * mm, "mid": v(31.87, 57.13) * mm, "end": v(31.41, 56.74) * mm});
            skArc(sketch, "E54.1.47.0", {"start": v(20.22, 61.59) * mm, "mid": v(20.18, 62.18) * mm, "end": v(19.73, 62.57) * mm});
            skLineSegment(sketch, "E54.4.47.0", {"start": v(19.63, 59.95) * mm, "end": v(20.22, 61.59) * mm});
            skArc(sketch, "E54.7.47.0", {"start": v(19.63, 59.95) * mm, "mid": v(19.66, 58.77) * mm, "end": v(19.78, 57.6) * mm});
            skArc(sketch, "E54.11.47.0", {"start": v(19.78, 57.6) * mm, "mid": v(19.94, 57.22) * mm, "end": v(20.27, 56.99) * mm});
            skLineSegment(sketch, "E54.15.47.0", {"start": v(20.27, 56.99) * mm, "end": v(20.65, 56.85) * mm});
            skLineSegment(sketch, "E54.18.47.0", {"start": v(21.02, 56.72) * mm, "end": v(20.65, 56.85) * mm});
            skArc(sketch, "E54.21.47.0", {"start": v(21.02, 56.72) * mm, "mid": v(21.43, 56.69) * mm, "end": v(21.8, 56.87) * mm});
            skArc(sketch, "E54.25.47.0", {"start": v(23.4, 58.59) * mm, "mid": v(22.63, 57.7) * mm, "end": v(21.8, 56.87) * mm});
            skLineSegment(sketch, "E54.29.47.0", {"start": v(23.4, 58.59) * mm, "end": v(24, 60.23) * mm});
            skArc(sketch, "E54.32.47.0", {"start": v(25, 60.67) * mm, "mid": v(24.4, 60.66) * mm, "end": v(24, 60.23) * mm});
            skArc(sketch, "E54.1.48.0", {"start": v(12.28, 63.63) * mm, "mid": v(12.17, 64.22) * mm, "end": v(11.67, 64.55) * mm});
            skLineSegment(sketch, "E54.4.48.0", {"start": v(11.9, 61.93) * mm, "end": v(12.28, 63.63) * mm});
            skArc(sketch, "E54.7.48.0", {"start": v(11.9, 61.93) * mm, "mid": v(12.08, 60.76) * mm, "end": v(12.35, 59.62) * mm});
            skArc(sketch, "E54.11.48.0", {"start": v(12.35, 59.62) * mm, "mid": v(12.55, 59.27) * mm, "end": v(12.91, 59.07) * mm});
            skLineSegment(sketch, "E54.15.48.0", {"start": v(12.91, 59.07) * mm, "end": v(13.3, 58.99) * mm});
            skLineSegment(sketch, "E54.18.48.0", {"start": v(13.69, 58.9) * mm, "end": v(13.3, 58.99) * mm});
            skArc(sketch, "E54.21.48.0", {"start": v(13.69, 58.9) * mm, "mid": v(14.1, 58.92) * mm, "end": v(14.44, 59.15) * mm});
            skArc(sketch, "E54.25.48.0", {"start": v(15.82, 61.05) * mm, "mid": v(15.16, 60.08) * mm, "end": v(14.44, 59.15) * mm});
            skLineSegment(sketch, "E54.29.48.0", {"start": v(15.82, 61.05) * mm, "end": v(16.2, 62.75) * mm});
            skArc(sketch, "E54.32.48.0", {"start": v(17.14, 63.32) * mm, "mid": v(16.55, 63.24) * mm, "end": v(16.2, 62.75) * mm});
            skArc(sketch, "E54.1.49.0", {"start": v(4.15, 64.66) * mm, "mid": v(3.97, 65.23) * mm, "end": v(3.43, 65.5) * mm});
            skLineSegment(sketch, "E54.4.49.0", {"start": v(3.99, 62.93) * mm, "end": v(4.15, 64.66) * mm});
            skArc(sketch, "E54.7.49.0", {"start": v(3.99, 62.93) * mm, "mid": v(4.31, 61.8) * mm, "end": v(4.72, 60.69) * mm});
            skArc(sketch, "E54.11.49.0", {"start": v(4.72, 60.69) * mm, "mid": v(4.97, 60.37) * mm, "end": v(5.35, 60.22) * mm});
            skLineSegment(sketch, "E54.15.49.0", {"start": v(5.35, 60.22) * mm, "end": v(5.75, 60.18) * mm});
            skLineSegment(sketch, "E54.18.49.0", {"start": v(6.14, 60.15) * mm, "end": v(5.75, 60.18) * mm});
            skArc(sketch, "E54.21.49.0", {"start": v(6.14, 60.15) * mm, "mid": v(6.54, 60.22) * mm, "end": v(6.85, 60.49) * mm});
            skArc(sketch, "E54.25.49.0", {"start": v(7.99, 62.55) * mm, "mid": v(7.46, 61.5) * mm, "end": v(6.85, 60.49) * mm});
            skLineSegment(sketch, "E54.29.49.0", {"start": v(7.99, 62.55) * mm, "end": v(8.15, 64.28) * mm});
            skArc(sketch, "E54.32.49.0", {"start": v(9.01, 64.97) * mm, "mid": v(8.44, 64.8) * mm, "end": v(8.15, 64.28) * mm});
            skArc(sketch, "E55.trimOffspring", {"start": v(-13.08, 64.27) * mm, "mid": v(-14.4, 64) * mm, "end": v(-15.7, 63.69) * mm});
            skArc(sketch, "E56.trimOffspring", {"start": v(-21.09, 62.12) * mm, "mid": v(-22.36, 61.68) * mm, "end": v(-23.62, 61.2) * mm});
            skArc(sketch, "E57.trimOffspring", {"start": v(-28.76, 58.98) * mm, "mid": v(-29.97, 58.38) * mm, "end": v(-31.16, 57.76) * mm});
            skArc(sketch, "E58.trimOffspring", {"start": v(-35.98, 54.9) * mm, "mid": v(-37.1, 54.16) * mm, "end": v(-38.21, 53.4) * mm});
            skArc(sketch, "E59.trimOffspring", {"start": v(-42.64, 49.96) * mm, "mid": v(-43.66, 49.08) * mm, "end": v(-44.66, 48.18) * mm});
            skArc(sketch, "E60.trimOffspring", {"start": v(-48.62, 44.22) * mm, "mid": v(-49.52, 43.22) * mm, "end": v(-50.4, 42.2) * mm});
            skArc(sketch, "E61.trimOffspring", {"start": v(-53.84, 37.77) * mm, "mid": v(-54.6, 36.66) * mm, "end": v(-55.35, 35.54) * mm});
            skArc(sketch, "E62.trimOffspring", {"start": v(-58.2, 30.72) * mm, "mid": v(-58.83, 29.52) * mm, "end": v(-59.43, 28.32) * mm});
            skArc(sketch, "E63.trimOffspring", {"start": v(-61.65, 23.17) * mm, "mid": v(-62.12, 21.91) * mm, "end": v(-62.56, 20.64) * mm});
            skArc(sketch, "E64.trimOffspring", {"start": v(-64.13, 15.26) * mm, "mid": v(-64.44, 13.95) * mm, "end": v(-64.72, 12.63) * mm});
            skArc(sketch, "E65.trimOffspring", {"start": v(-65.6, 7.1) * mm, "mid": v(-65.73, 5.76) * mm, "end": v(-65.85, 4.42) * mm});
            skArc(sketch, "E66.trimOffspring", {"start": v(-66.02, -1.19) * mm, "mid": v(-66, -2.53) * mm, "end": v(-65.94, -3.88) * mm});
            skArc(sketch, "E67.trimOffspring", {"start": v(-65.4, -9.46) * mm, "mid": v(-65.21, -10.79) * mm, "end": v(-64.99, -12.12) * mm});
            skArc(sketch, "E68.trimOffspring", {"start": v(-63.77, -17.59) * mm, "mid": v(-63.4, -18.88) * mm, "end": v(-63.01, -20.17) * mm});
            skArc(sketch, "E69.trimOffspring", {"start": v(-61.12, -25.44) * mm, "mid": v(-60.6, -26.68) * mm, "end": v(-60.05, -27.91) * mm});
            skArc(sketch, "E70.trimOffspring", {"start": v(-57.5, -32.9) * mm, "mid": v(-56.83, -34.07) * mm, "end": v(-56.13, -35.23) * mm});
            skArc(sketch, "E71.trimOffspring", {"start": v(-52.98, -39.86) * mm, "mid": v(-52.17, -40.93) * mm, "end": v(-51.33, -41.99) * mm});
            skArc(sketch, "E72.trimOffspring", {"start": v(-47.62, -46.2) * mm, "mid": v(-46.68, -47.15) * mm, "end": v(-45.72, -48.1) * mm});
            skArc(sketch, "E73.trimOffspring", {"start": v(-41.52, -51.8) * mm, "mid": v(-40.46, -52.64) * mm, "end": v(-39.4, -53.45) * mm});
            skArc(sketch, "E74.trimOffspring", {"start": v(-34.75, -56.6) * mm, "mid": v(-33.6, -57.3) * mm, "end": v(-32.44, -57.97) * mm});
            skArc(sketch, "E75.trimOffspring", {"start": v(-27.44, -60.52) * mm, "mid": v(-26.21, -61.07) * mm, "end": v(-24.97, -61.59) * mm});
            skArc(sketch, "E76.trimOffspring", {"start": v(-19.7, -63.49) * mm, "mid": v(-18.41, -63.87) * mm, "end": v(-17.11, -64.24) * mm});
            skArc(sketch, "E77.trimOffspring", {"start": v(-11.64, -65.46) * mm, "mid": v(-10.32, -65.68) * mm, "end": v(-8.99, -65.88) * mm});
            skArc(sketch, "E78.trimOffspring", {"start": v(-3.4, -66.4) * mm, "mid": v(-2.06, -66.46) * mm, "end": v(-0.71, -66.5) * mm});
            skArc(sketch, "E79.trimOffspring", {"start": v(4.89, -66.32) * mm, "mid": v(6.23, -66.2) * mm, "end": v(7.57, -66.06) * mm});
            skArc(sketch, "E80.trimOffspring", {"start": v(13.1, -65.19) * mm, "mid": v(14.42, -64.9) * mm, "end": v(15.73, -64.6) * mm});
            skArc(sketch, "E81.trimOffspring", {"start": v(21.11, -63.04) * mm, "mid": v(22.38, -62.6) * mm, "end": v(23.65, -62.12) * mm});
            skArc(sketch, "E82.trimOffspring", {"start": v(28.8, -59.9) * mm, "mid": v(30, -59.3) * mm, "end": v(31.19, -58.68) * mm});
            skArc(sketch, "E83.trimOffspring", {"start": v(36.01, -55.82) * mm, "mid": v(37.13, -55.08) * mm, "end": v(38.24, -54.3) * mm});
            skArc(sketch, "E84.trimOffspring", {"start": v(42.67, -50.87) * mm, "mid": v(43.69, -50) * mm, "end": v(44.69, -49.1) * mm});
            skArc(sketch, "E85.trimOffspring", {"start": v(48.65, -45.13) * mm, "mid": v(49.55, -44.13) * mm, "end": v(50.43, -43.11) * mm});
            skArc(sketch, "E86.trimOffspring", {"start": v(53.87, -38.68) * mm, "mid": v(54.63, -37.58) * mm, "end": v(55.38, -36.46) * mm});
            skArc(sketch, "E87.trimOffspring", {"start": v(58.23, -31.63) * mm, "mid": v(58.86, -30.44) * mm, "end": v(59.46, -29.23) * mm});
            skArc(sketch, "E88.trimOffspring", {"start": v(61.68, -24.09) * mm, "mid": v(62.15, -22.83) * mm, "end": v(62.6, -21.56) * mm});
            skArc(sketch, "E89.trimOffspring", {"start": v(64.16, -16.17) * mm, "mid": v(64.46, -14.86) * mm, "end": v(64.74, -13.55) * mm});
            skArc(sketch, "E90.trimOffspring", {"start": v(65.62, -8.01) * mm, "mid": v(65.76, -6.67) * mm, "end": v(65.87, -5.33) * mm});
            skArc(sketch, "E91.trimOffspring", {"start": v(66.05, 0.27) * mm, "mid": v(66.02, 1.62) * mm, "end": v(65.97, 2.96) * mm});
            skArc(sketch, "E92.trimOffspring", {"start": v(65.44, 8.54) * mm, "mid": v(65.24, 9.87) * mm, "end": v(65.02, 11.2) * mm});
            skArc(sketch, "E93.trimOffspring", {"start": v(63.8, 16.67) * mm, "mid": v(63.43, 17.97) * mm, "end": v(63.04, 19.26) * mm});
            skArc(sketch, "E94.trimOffspring", {"start": v(61.14, 24.53) * mm, "mid": v(60.62, 25.77) * mm, "end": v(60.08, 27) * mm});
            skArc(sketch, "E95.trimOffspring", {"start": v(57.53, 32) * mm, "mid": v(56.86, 33.16) * mm, "end": v(56.16, 34.31) * mm});
            skArc(sketch, "E96.trimOffspring", {"start": v(53.01, 38.95) * mm, "mid": v(52.2, 40.02) * mm, "end": v(51.36, 41.07) * mm});
            skArc(sketch, "E97.trimOffspring", {"start": v(47.65, 45.28) * mm, "mid": v(46.71, 46.24) * mm, "end": v(45.75, 47.18) * mm});
            skArc(sketch, "E98.trimOffspring", {"start": v(41.55, 50.89) * mm, "mid": v(40.5, 51.72) * mm, "end": v(39.42, 52.54) * mm});
            skArc(sketch, "E99.trimOffspring", {"start": v(34.78, 55.69) * mm, "mid": v(33.63, 56.39) * mm, "end": v(32.47, 57.06) * mm});
            skArc(sketch, "E100.trimOffspring", {"start": v(27.47, 59.6) * mm, "mid": v(26.24, 60.15) * mm, "end": v(25, 60.67) * mm});
            skArc(sketch, "E101.trimOffspring", {"start": v(19.73, 62.57) * mm, "mid": v(18.44, 62.96) * mm, "end": v(17.14, 63.32) * mm});
            skArc(sketch, "E102.trimOffspring", {"start": v(11.67, 64.55) * mm, "mid": v(10.35, 64.77) * mm, "end": v(9.01, 64.97) * mm});
            skArc(sketch, "E103.trimOffspring", {"start": v(3.43, 65.5) * mm, "mid": v(2.09, 65.55) * mm, "end": v(0.74, 65.58) * mm});
            skSolve(sketch);
        }
        {
            var Q0;
            Q0=makeQuery(id+"F0.imprint","IMPRINT",FACE,{"disambiguationData":[TD([[makeQuery(id+"F0.imprint","IMPRINT",EDGE,{"derivedFrom":sQuery(id+"F0.wireOp",EDGE,"E0")}),1.0]])]});
            extrude(context, id + "F1", {"entities" : qUnion([Q0]), "depth" : 127 * mm});
        }
    });
